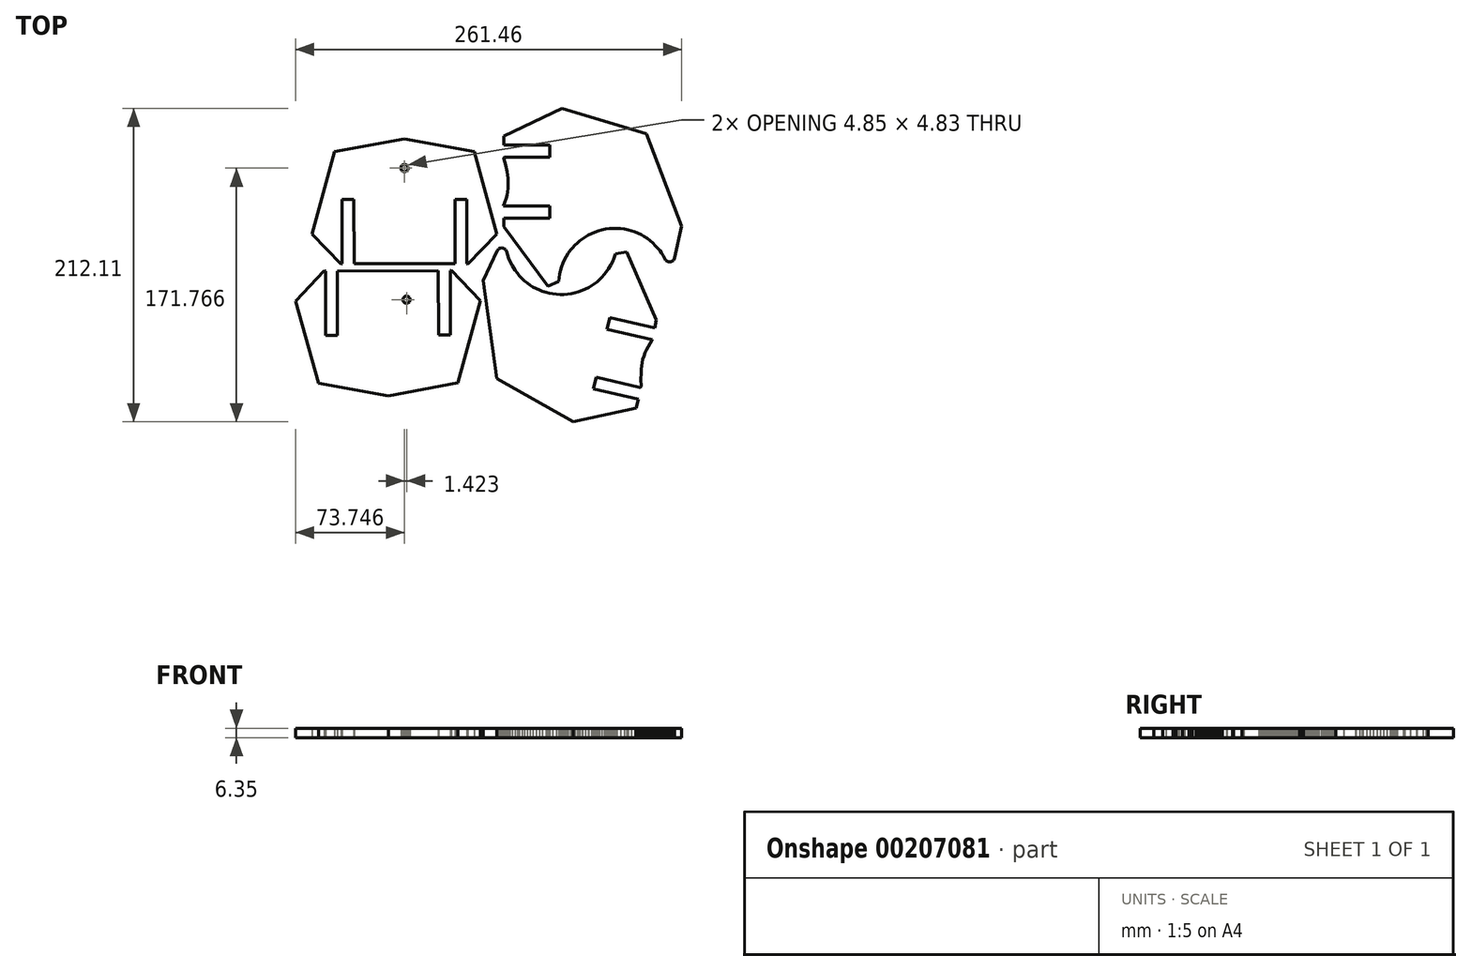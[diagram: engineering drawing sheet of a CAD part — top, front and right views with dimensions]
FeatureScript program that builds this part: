
annotation { "Feature Type Name" : "Feature", "Feature Type Description" : "" }
export const myFeature = defineFeature(function(context is Context, id is Id, definition is map)
    precondition{}
    {
        {
            var Q0;
            Q0=qCreatedBy(makeId("Top.planeOp"),FACE);
            var sketch = newSketch(context, id + "F0", { "sketchPlane" : qUnion([Q0])});
            skLineSegment(sketch, "E0", {"start": v(-798.32, 30.2) * mm, "end": v(-878.98, 30.2) * mm});
            skLineSegment(sketch, "E1", {"start": v(-854.84, 105.1) * mm, "end": v(-865.97, 116.25) * mm});
            skArc(sketch, "E2", {"start": v(-798.32, 30.2) * mm, "mid": v(-791.28, 34.9) * mm, "end": v(-792.93, 43.2) * mm});
            skArc(sketch, "E3", {"start": v(-865.97, 116.25) * mm, "mid": v(-874.28, 117.9) * mm, "end": v(-878.98, 110.86) * mm});
            skLineSegment(sketch, "E4", {"start": v(-878.98, 110.86) * mm, "end": v(-878.98, 30.2) * mm});
            skArc(sketch, "E5", {"start": v(-854.84, 105.1) * mm, "mid": v(-851.3, 103.1) * mm, "end": v(-847.23, 103.2) * mm});
            skArc(sketch, "E6", {"start": v(-805.97, 61.95) * mm, "mid": v(-814.21, 94.96) * mm, "end": v(-847.23, 103.2) * mm});
            skArc(sketch, "E7", {"start": v(-851.35, 42.59) * mm, "mid": v(-846.9, 52.27) * mm, "end": v(-846.27, 62.9) * mm});
            skLineSegment(sketch, "E8", {"start": v(-831.03, 42.59) * mm, "end": v(-851.35, 42.59) * mm});
            skArc(sketch, "E9", {"start": v(-836.11, 62.9) * mm, "mid": v(-835.49, 52.27) * mm, "end": v(-831.03, 42.59) * mm});
            skArc(sketch, "E10", {"start": v(-815.8, 57.83) * mm, "mid": v(-825.47, 62.28) * mm, "end": v(-836.11, 62.9) * mm});
            skLineSegment(sketch, "E11", {"start": v(-815.8, 78.15) * mm, "end": v(-815.8, 57.83) * mm});
            skArc(sketch, "E12", {"start": v(-836.11, 73.07) * mm, "mid": v(-825.47, 73.69) * mm, "end": v(-815.8, 78.15) * mm});
            skArc(sketch, "E13", {"start": v(-831.03, 93.39) * mm, "mid": v(-835.49, 83.7) * mm, "end": v(-836.11, 73.07) * mm});
            skLineSegment(sketch, "E14", {"start": v(-851.35, 93.39) * mm, "end": v(-831.03, 93.39) * mm});
            skArc(sketch, "E15", {"start": v(-846.27, 73.07) * mm, "mid": v(-846.9, 83.7) * mm, "end": v(-851.35, 93.39) * mm});
            skArc(sketch, "E16", {"start": v(-866.6, 78.15) * mm, "mid": v(-856.91, 73.69) * mm, "end": v(-846.27, 73.07) * mm});
            skLineSegment(sketch, "E17", {"start": v(-866.6, 57.83) * mm, "end": v(-866.6, 78.15) * mm});
            skArc(sketch, "E18", {"start": v(-846.27, 62.9) * mm, "mid": v(-856.91, 62.28) * mm, "end": v(-866.6, 57.83) * mm});
            skArc(sketch, "E19", {"start": v(-805.97, 61.95) * mm, "mid": v(-806.07, 57.88) * mm, "end": v(-804.07, 54.34) * mm});
            skLineSegment(sketch, "E20", {"start": v(-804.07, 54.34) * mm, "end": v(-792.93, 43.2) * mm});
            skLineSegment(sketch, "E21", {"start": v(-610.3, 30.2) * mm, "end": v(-699.5, 30.2) * mm});
            skLineSegment(sketch, "E22", {"start": v(-661.26, 120.9) * mm, "end": v(-660.25, 121.09) * mm});
            skLineSegment(sketch, "E23", {"start": v(-660.57, 87.06) * mm, "end": v(-661.8, 88.46) * mm});
            skLineSegment(sketch, "E24", {"start": v(-668.38, 97.43) * mm, "end": v(-660.94, 110.33) * mm});
            skLineSegment(sketch, "E25", {"start": v(-651.07, 70.5) * mm, "end": v(-663.11, 63.55) * mm});
            skLineSegment(sketch, "E26", {"start": v(-661.79, 79.2) * mm, "end": v(-660.35, 77.84) * mm});
            skLineSegment(sketch, "E27", {"start": v(-661.05, 36.54) * mm, "end": v(-674.5, 36.54) * mm});
            skLineSegment(sketch, "E28", {"start": v(-661.84, 38.75) * mm, "end": v(-661.05, 36.54) * mm});
            skLineSegment(sketch, "E29", {"start": v(-712.2, 42.9) * mm, "end": v(-712.2, 132.5) * mm});
            skLineSegment(sketch, "E30", {"start": v(-668.24, 67.85) * mm, "end": v(-669.88, 69.36) * mm});
            skLineSegment(sketch, "E31", {"start": v(-679.21, 69.81) * mm, "end": v(-677.61, 68.1) * mm});
            skLineSegment(sketch, "E32", {"start": v(-689, 61.7) * mm, "end": v(-682.28, 73.35) * mm});
            skLineSegment(sketch, "E33", {"start": v(-705.86, 68) * mm, "end": v(-705.86, 81.45) * mm});
            skLineSegment(sketch, "E34", {"start": v(-687.72, 76.63) * mm, "end": v(-694.45, 64.97) * mm});
            skLineSegment(sketch, "E35", {"start": v(-708.77, 34.2) * mm, "end": v(-709.3, 34.8) * mm});
            skLineSegment(sketch, "E36", {"start": v(-712.1, 41.3) * mm, "end": v(-712.18, 42.1) * mm});
            skLineSegment(sketch, "E37", {"start": v(-710.64, 36.78) * mm, "end": v(-711, 37.49) * mm});
            skLineSegment(sketch, "E38", {"start": v(-710.23, 36.09) * mm, "end": v(-710.64, 36.78) * mm});
            skLineSegment(sketch, "E39", {"start": v(-709.78, 35.43) * mm, "end": v(-710.23, 36.09) * mm});
            skLineSegment(sketch, "E40", {"start": v(-709.3, 34.8) * mm, "end": v(-709.78, 35.43) * mm});
            skLineSegment(sketch, "E41", {"start": v(-711.81, 39.74) * mm, "end": v(-711.98, 40.51) * mm});
            skLineSegment(sketch, "E42", {"start": v(-711.98, 40.51) * mm, "end": v(-712.1, 41.3) * mm});
            skLineSegment(sketch, "E43", {"start": v(-711.59, 38.97) * mm, "end": v(-711.81, 39.74) * mm});
            skLineSegment(sketch, "E44", {"start": v(-711.32, 38.22) * mm, "end": v(-711.59, 38.97) * mm});
            skLineSegment(sketch, "E45", {"start": v(-711, 37.49) * mm, "end": v(-711.32, 38.22) * mm});
            skLineSegment(sketch, "E46", {"start": v(-712.18, 42.1) * mm, "end": v(-712.2, 42.9) * mm});
            skLineSegment(sketch, "E47", {"start": v(-706.97, 32.62) * mm, "end": v(-707.6, 33.1) * mm});
            skLineSegment(sketch, "E48", {"start": v(-702.67, 30.6) * mm, "end": v(-703.43, 30.82) * mm});
            skLineSegment(sketch, "E49", {"start": v(-705.63, 31.76) * mm, "end": v(-706.31, 32.17) * mm});
            skLineSegment(sketch, "E50", {"start": v(-706.31, 32.17) * mm, "end": v(-706.97, 32.62) * mm});
            skLineSegment(sketch, "E51", {"start": v(-704.92, 31.4) * mm, "end": v(-705.63, 31.76) * mm});
            skLineSegment(sketch, "E52", {"start": v(-704.18, 31.09) * mm, "end": v(-704.92, 31.4) * mm});
            skLineSegment(sketch, "E53", {"start": v(-703.43, 30.82) * mm, "end": v(-704.18, 31.09) * mm});
            skLineSegment(sketch, "E54", {"start": v(-699.5, 30.2) * mm, "end": v(-700.3, 30.22) * mm});
            skLineSegment(sketch, "E55", {"start": v(-701.89, 30.42) * mm, "end": v(-702.67, 30.6) * mm});
            skLineSegment(sketch, "E56", {"start": v(-701.1, 30.3) * mm, "end": v(-701.89, 30.42) * mm});
            skLineSegment(sketch, "E57", {"start": v(-700.3, 30.22) * mm, "end": v(-701.1, 30.3) * mm});
            skLineSegment(sketch, "E58", {"start": v(-684.11, 56.62) * mm, "end": v(-685.78, 58.28) * mm});
            skLineSegment(sketch, "E59", {"start": v(-708.2, 33.64) * mm, "end": v(-708.77, 34.2) * mm});
            skLineSegment(sketch, "E60", {"start": v(-707.6, 33.1) * mm, "end": v(-708.2, 33.64) * mm});
            skLineSegment(sketch, "E61", {"start": v(-696.76, 65.48) * mm, "end": v(-699.05, 66.04) * mm});
            skLineSegment(sketch, "E62", {"start": v(-701.34, 66.64) * mm, "end": v(-703.6, 67.3) * mm});
            skLineSegment(sketch, "E63", {"start": v(-703.6, 67.3) * mm, "end": v(-705.86, 68) * mm});
            skLineSegment(sketch, "E64", {"start": v(-699.05, 66.04) * mm, "end": v(-701.34, 66.64) * mm});
            skLineSegment(sketch, "E65", {"start": v(-685.78, 58.28) * mm, "end": v(-687.41, 59.98) * mm});
            skLineSegment(sketch, "E66", {"start": v(-694.45, 64.97) * mm, "end": v(-696.76, 65.48) * mm});
            skLineSegment(sketch, "E67", {"start": v(-687.41, 59.98) * mm, "end": v(-689, 61.7) * mm});
            skLineSegment(sketch, "E68", {"start": v(-677.55, 47.88) * mm, "end": v(-665.9, 54.6) * mm});
            skLineSegment(sketch, "E69", {"start": v(-665.5, 52.3) * mm, "end": v(-665.02, 50) * mm});
            skLineSegment(sketch, "E70", {"start": v(-675.87, 41.04) * mm, "end": v(-676.48, 43.3) * mm});
            skLineSegment(sketch, "E71", {"start": v(-674.5, 36.54) * mm, "end": v(-675.21, 38.78) * mm});
            skLineSegment(sketch, "E72", {"start": v(-675.21, 38.78) * mm, "end": v(-675.87, 41.04) * mm});
            skLineSegment(sketch, "E73", {"start": v(-677.04, 45.59) * mm, "end": v(-677.55, 47.88) * mm});
            skLineSegment(sketch, "E74", {"start": v(-676.48, 43.3) * mm, "end": v(-677.04, 45.59) * mm});
            skLineSegment(sketch, "E75", {"start": v(-663.28, 43.2) * mm, "end": v(-662.59, 40.96) * mm});
            skLineSegment(sketch, "E76", {"start": v(-662.59, 40.96) * mm, "end": v(-661.84, 38.75) * mm});
            skLineSegment(sketch, "E77", {"start": v(-664.5, 47.72) * mm, "end": v(-663.91, 45.46) * mm});
            skLineSegment(sketch, "E78", {"start": v(-663.91, 45.46) * mm, "end": v(-663.28, 43.2) * mm});
            skLineSegment(sketch, "E79", {"start": v(-665.02, 50) * mm, "end": v(-664.5, 47.72) * mm});
            skLineSegment(sketch, "E80", {"start": v(-669.02, 60.14) * mm, "end": v(-680.68, 53.4) * mm});
            skLineSegment(sketch, "E81", {"start": v(-674.29, 64.8) * mm, "end": v(-672.57, 63.2) * mm});
            skLineSegment(sketch, "E82", {"start": v(-682.41, 55) * mm, "end": v(-684.11, 56.62) * mm});
            skLineSegment(sketch, "E83", {"start": v(-680.68, 53.4) * mm, "end": v(-682.41, 55) * mm});
            skLineSegment(sketch, "E84", {"start": v(-677.61, 68.1) * mm, "end": v(-675.97, 66.43) * mm});
            skLineSegment(sketch, "E85", {"start": v(-675.97, 66.43) * mm, "end": v(-674.29, 64.8) * mm});
            skLineSegment(sketch, "E86", {"start": v(-665.9, 54.6) * mm, "end": v(-665.5, 52.3) * mm});
            skLineSegment(sketch, "E87", {"start": v(-666.57, 66.37) * mm, "end": v(-668.24, 67.85) * mm});
            skLineSegment(sketch, "E88", {"start": v(-670.81, 61.65) * mm, "end": v(-669.02, 60.14) * mm});
            skLineSegment(sketch, "E89", {"start": v(-672.57, 63.2) * mm, "end": v(-670.81, 61.65) * mm});
            skLineSegment(sketch, "E90", {"start": v(-663.11, 63.55) * mm, "end": v(-664.86, 64.94) * mm});
            skLineSegment(sketch, "E91", {"start": v(-664.86, 64.94) * mm, "end": v(-666.57, 66.37) * mm});
            skLineSegment(sketch, "E92", {"start": v(-709.16, 135.2) * mm, "end": v(-708.36, 134.41) * mm});
            skLineSegment(sketch, "E93", {"start": v(-712.2, 132.5) * mm, "end": v(-711.43, 133.15) * mm});
            skLineSegment(sketch, "E94", {"start": v(-709.9, 134.5) * mm, "end": v(-709.16, 135.2) * mm});
            skLineSegment(sketch, "E95", {"start": v(-710.66, 133.82) * mm, "end": v(-709.9, 134.5) * mm});
            skLineSegment(sketch, "E96", {"start": v(-711.43, 133.15) * mm, "end": v(-710.66, 133.82) * mm});
            skLineSegment(sketch, "E97", {"start": v(-673.78, 100.78) * mm, "end": v(-666.3, 113.73) * mm});
            skLineSegment(sketch, "E98", {"start": v(-695.65, 104.76) * mm, "end": v(-693.89, 104.17) * mm});
            skLineSegment(sketch, "E99", {"start": v(-683.25, 95.22) * mm, "end": v(-685.2, 95.53) * mm});
            skLineSegment(sketch, "E100", {"start": v(-686.52, 82.87) * mm, "end": v(-684.31, 82.54) * mm});
            skLineSegment(sketch, "E101", {"start": v(-686.7, 102.27) * mm, "end": v(-684.87, 101.92) * mm});
            skLineSegment(sketch, "E102", {"start": v(-701.67, 86.69) * mm, "end": v(-699.55, 85.98) * mm});
            skLineSegment(sketch, "E103", {"start": v(-697.91, 78.87) * mm, "end": v(-695.9, 78.34) * mm});
            skLineSegment(sketch, "E104", {"start": v(-697.41, 85.33) * mm, "end": v(-695.26, 84.73) * mm});
            skLineSegment(sketch, "E105", {"start": v(-703.9, 80.74) * mm, "end": v(-701.91, 80.07) * mm});
            skLineSegment(sketch, "E106", {"start": v(-705.86, 81.45) * mm, "end": v(-703.9, 80.74) * mm});
            skLineSegment(sketch, "E107", {"start": v(-699.92, 79.45) * mm, "end": v(-697.91, 78.87) * mm});
            skLineSegment(sketch, "E108", {"start": v(-701.91, 80.07) * mm, "end": v(-699.92, 79.45) * mm});
            skLineSegment(sketch, "E109", {"start": v(-699.55, 85.98) * mm, "end": v(-697.41, 85.33) * mm});
            skLineSegment(sketch, "E110", {"start": v(-693.87, 77.85) * mm, "end": v(-691.83, 77.4) * mm});
            skLineSegment(sketch, "E111", {"start": v(-691.83, 77.4) * mm, "end": v(-689.78, 77) * mm});
            skLineSegment(sketch, "E112", {"start": v(-689.78, 77) * mm, "end": v(-687.72, 76.63) * mm});
            skLineSegment(sketch, "E113", {"start": v(-693.1, 84.19) * mm, "end": v(-690.91, 83.7) * mm});
            skLineSegment(sketch, "E114", {"start": v(-695.9, 78.34) * mm, "end": v(-693.87, 77.85) * mm});
            skLineSegment(sketch, "E115", {"start": v(-695.26, 84.73) * mm, "end": v(-693.1, 84.19) * mm});
            skLineSegment(sketch, "E116", {"start": v(-688.72, 83.26) * mm, "end": v(-686.52, 82.87) * mm});
            skLineSegment(sketch, "E117", {"start": v(-690.91, 83.7) * mm, "end": v(-688.72, 83.26) * mm});
            skLineSegment(sketch, "E118", {"start": v(-696.7, 98.41) * mm, "end": v(-698.57, 99.06) * mm});
            skLineSegment(sketch, "E119", {"start": v(-705.86, 102.13) * mm, "end": v(-705.86, 88.25) * mm});
            skLineSegment(sketch, "E120", {"start": v(-703.78, 87.45) * mm, "end": v(-701.67, 86.69) * mm});
            skLineSegment(sketch, "E121", {"start": v(-705.86, 88.25) * mm, "end": v(-703.78, 87.45) * mm});
            skLineSegment(sketch, "E122", {"start": v(-702.25, 100.5) * mm, "end": v(-704.07, 101.3) * mm});
            skLineSegment(sketch, "E123", {"start": v(-704.07, 101.3) * mm, "end": v(-705.86, 102.13) * mm});
            skLineSegment(sketch, "E124", {"start": v(-700.42, 99.76) * mm, "end": v(-702.25, 100.5) * mm});
            skLineSegment(sketch, "E125", {"start": v(-698.57, 99.06) * mm, "end": v(-700.42, 99.76) * mm});
            skLineSegment(sketch, "E126", {"start": v(-689.09, 96.3) * mm, "end": v(-691, 96.75) * mm});
            skLineSegment(sketch, "E127", {"start": v(-692.11, 103.63) * mm, "end": v(-690.32, 103.13) * mm});
            skLineSegment(sketch, "E128", {"start": v(-692.92, 97.26) * mm, "end": v(-694.82, 97.81) * mm});
            skLineSegment(sketch, "E129", {"start": v(-694.82, 97.81) * mm, "end": v(-696.7, 98.41) * mm});
            skLineSegment(sketch, "E130", {"start": v(-691, 96.75) * mm, "end": v(-692.92, 97.26) * mm});
            skLineSegment(sketch, "E131", {"start": v(-693.89, 104.17) * mm, "end": v(-692.11, 103.63) * mm});
            skLineSegment(sketch, "E132", {"start": v(-687.15, 95.89) * mm, "end": v(-689.09, 96.3) * mm});
            skLineSegment(sketch, "E133", {"start": v(-685.2, 95.53) * mm, "end": v(-687.15, 95.89) * mm});
            skLineSegment(sketch, "E134", {"start": v(-688.51, 102.68) * mm, "end": v(-686.7, 102.27) * mm});
            skLineSegment(sketch, "E135", {"start": v(-690.32, 103.13) * mm, "end": v(-688.51, 102.68) * mm});
            skLineSegment(sketch, "E136", {"start": v(-669.64, 88.06) * mm, "end": v(-668.42, 86.5) * mm});
            skLineSegment(sketch, "E137", {"start": v(-678.88, 79.25) * mm, "end": v(-671.94, 91.27) * mm});
            skLineSegment(sketch, "E138", {"start": v(-684.31, 82.54) * mm, "end": v(-677.36, 94.59) * mm});
            skLineSegment(sketch, "E139", {"start": v(-673.04, 72.5) * mm, "end": v(-674.56, 74.14) * mm});
            skLineSegment(sketch, "E140", {"start": v(-677.48, 77.51) * mm, "end": v(-678.88, 79.25) * mm});
            skLineSegment(sketch, "E141", {"start": v(-682.28, 73.35) * mm, "end": v(-680.77, 71.56) * mm});
            skLineSegment(sketch, "E142", {"start": v(-680.77, 71.56) * mm, "end": v(-679.21, 69.81) * mm});
            skLineSegment(sketch, "E143", {"start": v(-676.04, 75.8) * mm, "end": v(-677.48, 77.51) * mm});
            skLineSegment(sketch, "E144", {"start": v(-674.56, 74.14) * mm, "end": v(-676.04, 75.8) * mm});
            skLineSegment(sketch, "E145", {"start": v(-669.88, 69.36) * mm, "end": v(-671.48, 70.91) * mm});
            skLineSegment(sketch, "E146", {"start": v(-671.48, 70.91) * mm, "end": v(-673.04, 72.5) * mm});
            skLineSegment(sketch, "E147", {"start": v(-668.42, 86.5) * mm, "end": v(-667.17, 84.98) * mm});
            skLineSegment(sketch, "E148", {"start": v(-665.88, 83.48) * mm, "end": v(-664.55, 82.02) * mm});
            skLineSegment(sketch, "E149", {"start": v(-664.55, 82.02) * mm, "end": v(-663.19, 80.6) * mm});
            skLineSegment(sketch, "E150", {"start": v(-663.19, 80.6) * mm, "end": v(-661.79, 79.2) * mm});
            skLineSegment(sketch, "E151", {"start": v(-667.17, 84.98) * mm, "end": v(-665.88, 83.48) * mm});
            skLineSegment(sketch, "E152", {"start": v(-677.36, 94.59) * mm, "end": v(-679.33, 94.75) * mm});
            skLineSegment(sketch, "E153", {"start": v(-681.3, 94.96) * mm, "end": v(-683.25, 95.22) * mm});
            skLineSegment(sketch, "E154", {"start": v(-679.33, 94.75) * mm, "end": v(-681.3, 94.96) * mm});
            skLineSegment(sketch, "E155", {"start": v(-679.35, 101.13) * mm, "end": v(-677.5, 100.96) * mm});
            skLineSegment(sketch, "E156", {"start": v(-683.04, 101.6) * mm, "end": v(-681.2, 101.35) * mm});
            skLineSegment(sketch, "E157", {"start": v(-684.87, 101.92) * mm, "end": v(-683.04, 101.6) * mm});
            skLineSegment(sketch, "E158", {"start": v(-681.2, 101.35) * mm, "end": v(-679.35, 101.13) * mm});
            skLineSegment(sketch, "E159", {"start": v(-677.5, 100.96) * mm, "end": v(-675.64, 100.85) * mm});
            skLineSegment(sketch, "E160", {"start": v(-675.64, 100.85) * mm, "end": v(-673.78, 100.78) * mm});
            skLineSegment(sketch, "E161", {"start": v(-666.34, 94.33) * mm, "end": v(-667.38, 95.87) * mm});
            skLineSegment(sketch, "E162", {"start": v(-671.94, 91.27) * mm, "end": v(-670.8, 89.65) * mm});
            skLineSegment(sketch, "E163", {"start": v(-670.8, 89.65) * mm, "end": v(-669.64, 88.06) * mm});
            skLineSegment(sketch, "E164", {"start": v(-662.99, 89.88) * mm, "end": v(-664.14, 91.33) * mm});
            skLineSegment(sketch, "E165", {"start": v(-661.8, 88.46) * mm, "end": v(-662.99, 89.88) * mm});
            skLineSegment(sketch, "E166", {"start": v(-664.14, 91.33) * mm, "end": v(-665.26, 92.82) * mm});
            skLineSegment(sketch, "E167", {"start": v(-665.26, 92.82) * mm, "end": v(-666.34, 94.33) * mm});
            skLineSegment(sketch, "E168", {"start": v(-667.38, 95.87) * mm, "end": v(-668.38, 97.43) * mm});
            skLineSegment(sketch, "E169", {"start": v(-686.12, 121.73) * mm, "end": v(-684.57, 121.32) * mm});
            skLineSegment(sketch, "E170", {"start": v(-683.62, 114.6) * mm, "end": v(-685.32, 114.98) * mm});
            skLineSegment(sketch, "E171", {"start": v(-689.2, 122.69) * mm, "end": v(-687.66, 122.19) * mm});
            skLineSegment(sketch, "E172", {"start": v(-705.86, 124.13) * mm, "end": v(-705.86, 109.25) * mm});
            skLineSegment(sketch, "E173", {"start": v(-702.95, 122.22) * mm, "end": v(-704.42, 123.16) * mm});
            skLineSegment(sketch, "E174", {"start": v(-696.82, 118.93) * mm, "end": v(-698.4, 119.68) * mm});
            skLineSegment(sketch, "E175", {"start": v(-697.4, 105.4) * mm, "end": v(-695.65, 104.76) * mm});
            skLineSegment(sketch, "E176", {"start": v(-704.2, 108.4) * mm, "end": v(-702.54, 107.58) * mm});
            skLineSegment(sketch, "E177", {"start": v(-705.86, 109.25) * mm, "end": v(-704.2, 108.4) * mm});
            skLineSegment(sketch, "E178", {"start": v(-700.84, 106.8) * mm, "end": v(-699.13, 106.08) * mm});
            skLineSegment(sketch, "E179", {"start": v(-702.54, 107.58) * mm, "end": v(-700.84, 106.8) * mm});
            skLineSegment(sketch, "E180", {"start": v(-699.13, 106.08) * mm, "end": v(-697.4, 105.4) * mm});
            skLineSegment(sketch, "E181", {"start": v(-701.46, 121.33) * mm, "end": v(-702.95, 122.22) * mm});
            skLineSegment(sketch, "E182", {"start": v(-698.4, 119.68) * mm, "end": v(-699.94, 120.48) * mm});
            skLineSegment(sketch, "E183", {"start": v(-699.94, 120.48) * mm, "end": v(-701.46, 121.33) * mm});
            skLineSegment(sketch, "E184", {"start": v(-690.35, 116.38) * mm, "end": v(-692, 116.94) * mm});
            skLineSegment(sketch, "E185", {"start": v(-693.62, 117.56) * mm, "end": v(-695.23, 118.22) * mm});
            skLineSegment(sketch, "E186", {"start": v(-692, 116.94) * mm, "end": v(-693.62, 117.56) * mm});
            skLineSegment(sketch, "E187", {"start": v(-695.23, 118.22) * mm, "end": v(-696.82, 118.93) * mm});
            skLineSegment(sketch, "E188", {"start": v(-687.01, 115.4) * mm, "end": v(-688.69, 115.86) * mm});
            skLineSegment(sketch, "E189", {"start": v(-688.69, 115.86) * mm, "end": v(-690.35, 116.38) * mm});
            skLineSegment(sketch, "E190", {"start": v(-685.32, 114.98) * mm, "end": v(-687.01, 115.4) * mm});
            skLineSegment(sketch, "E191", {"start": v(-687.66, 122.19) * mm, "end": v(-686.12, 121.73) * mm});
            skLineSegment(sketch, "E192", {"start": v(-697.96, 126.65) * mm, "end": v(-696.55, 125.87) * mm});
            skLineSegment(sketch, "E193", {"start": v(-705.86, 132.13) * mm, "end": v(-704.61, 131.12) * mm});
            skLineSegment(sketch, "E194", {"start": v(-703.34, 130.14) * mm, "end": v(-702.03, 129.2) * mm});
            skLineSegment(sketch, "E195", {"start": v(-704.42, 123.16) * mm, "end": v(-705.86, 124.13) * mm});
            skLineSegment(sketch, "E196", {"start": v(-704.61, 131.12) * mm, "end": v(-703.34, 130.14) * mm});
            skLineSegment(sketch, "E197", {"start": v(-699.34, 127.46) * mm, "end": v(-697.96, 126.65) * mm});
            skLineSegment(sketch, "E198", {"start": v(-700.7, 128.31) * mm, "end": v(-699.34, 127.46) * mm});
            skLineSegment(sketch, "E199", {"start": v(-702.03, 129.2) * mm, "end": v(-700.7, 128.31) * mm});
            skLineSegment(sketch, "E200", {"start": v(-706.7, 132.88) * mm, "end": v(-705.86, 132.13) * mm});
            skLineSegment(sketch, "E201", {"start": v(-707.54, 133.64) * mm, "end": v(-706.7, 132.88) * mm});
            skLineSegment(sketch, "E202", {"start": v(-708.36, 134.41) * mm, "end": v(-707.54, 133.64) * mm});
            skLineSegment(sketch, "E203", {"start": v(-692.2, 123.83) * mm, "end": v(-690.7, 123.23) * mm});
            skLineSegment(sketch, "E204", {"start": v(-695.12, 125.15) * mm, "end": v(-693.67, 124.47) * mm});
            skLineSegment(sketch, "E205", {"start": v(-696.55, 125.87) * mm, "end": v(-695.12, 125.15) * mm});
            skLineSegment(sketch, "E206", {"start": v(-693.67, 124.47) * mm, "end": v(-692.2, 123.83) * mm});
            skLineSegment(sketch, "E207", {"start": v(-690.7, 123.23) * mm, "end": v(-689.2, 122.69) * mm});
            skLineSegment(sketch, "E208", {"start": v(-673.45, 119.82) * mm, "end": v(-671.85, 119.8) * mm});
            skLineSegment(sketch, "E209", {"start": v(-671.52, 113.46) * mm, "end": v(-673.26, 113.47) * mm});
            skLineSegment(sketch, "E210", {"start": v(-679.85, 120.4) * mm, "end": v(-678.26, 120.18) * mm});
            skLineSegment(sketch, "E211", {"start": v(-678.46, 113.8) * mm, "end": v(-680.2, 114.02) * mm});
            skLineSegment(sketch, "E212", {"start": v(-681.91, 114.3) * mm, "end": v(-683.62, 114.6) * mm});
            skLineSegment(sketch, "E213", {"start": v(-680.2, 114.02) * mm, "end": v(-681.91, 114.3) * mm});
            skLineSegment(sketch, "E214", {"start": v(-683, 120.97) * mm, "end": v(-681.43, 120.65) * mm});
            skLineSegment(sketch, "E215", {"start": v(-684.57, 121.32) * mm, "end": v(-683, 120.97) * mm});
            skLineSegment(sketch, "E216", {"start": v(-681.43, 120.65) * mm, "end": v(-679.85, 120.4) * mm});
            skLineSegment(sketch, "E217", {"start": v(-675, 113.53) * mm, "end": v(-676.73, 113.64) * mm});
            skLineSegment(sketch, "E218", {"start": v(-676.73, 113.64) * mm, "end": v(-678.46, 113.8) * mm});
            skLineSegment(sketch, "E219", {"start": v(-673.26, 113.47) * mm, "end": v(-675, 113.53) * mm});
            skLineSegment(sketch, "E220", {"start": v(-676.66, 120) * mm, "end": v(-675.06, 119.9) * mm});
            skLineSegment(sketch, "E221", {"start": v(-678.26, 120.18) * mm, "end": v(-676.66, 120) * mm});
            skLineSegment(sketch, "E222", {"start": v(-675.06, 119.9) * mm, "end": v(-673.45, 119.82) * mm});
            skLineSegment(sketch, "E223", {"start": v(-668.64, 119.91) * mm, "end": v(-667.04, 120.04) * mm});
            skLineSegment(sketch, "E224", {"start": v(-666.3, 113.73) * mm, "end": v(-668.04, 113.59) * mm});
            skLineSegment(sketch, "E225", {"start": v(-669.78, 113.5) * mm, "end": v(-671.52, 113.46) * mm});
            skLineSegment(sketch, "E226", {"start": v(-668.04, 113.59) * mm, "end": v(-669.78, 113.5) * mm});
            skLineSegment(sketch, "E227", {"start": v(-670.24, 119.83) * mm, "end": v(-668.64, 119.91) * mm});
            skLineSegment(sketch, "E228", {"start": v(-671.85, 119.8) * mm, "end": v(-670.24, 119.83) * mm});
            skLineSegment(sketch, "E229", {"start": v(-665.44, 120.22) * mm, "end": v(-663.85, 120.44) * mm});
            skLineSegment(sketch, "E230", {"start": v(-667.04, 120.04) * mm, "end": v(-665.44, 120.22) * mm});
            skLineSegment(sketch, "E231", {"start": v(-662.27, 120.71) * mm, "end": v(-661.26, 120.9) * mm});
            skLineSegment(sketch, "E232", {"start": v(-663.85, 120.44) * mm, "end": v(-662.27, 120.71) * mm});
            skLineSegment(sketch, "E233", {"start": v(-622.8, 70.18) * mm, "end": v(-622.76, 68.54) * mm});
            skLineSegment(sketch, "E234", {"start": v(-629.13, 69.02) * mm, "end": v(-629.05, 67.28) * mm});
            skLineSegment(sketch, "E235", {"start": v(-641.82, 68.51) * mm, "end": v(-628.92, 75.96) * mm});
            skLineSegment(sketch, "E236", {"start": v(-614.47, 42.28) * mm, "end": v(-613.56, 40.91) * mm});
            skLineSegment(sketch, "E237", {"start": v(-637.07, 44.97) * mm, "end": v(-637.72, 46.7) * mm});
            skLineSegment(sketch, "E238", {"start": v(-638.87, 50.24) * mm, "end": v(-639.38, 52.02) * mm});
            skLineSegment(sketch, "E239", {"start": v(-658.33, 49.26) * mm, "end": v(-658.83, 51.43) * mm});
            skLineSegment(sketch, "E240", {"start": v(-645.76, 51.34) * mm, "end": v(-645.25, 49.43) * mm});
            skLineSegment(sketch, "E241", {"start": v(-640.33, 36.54) * mm, "end": v(-654.23, 36.54) * mm});
            skLineSegment(sketch, "E242", {"start": v(-655.8, 40.71) * mm, "end": v(-656.51, 42.82) * mm});
            skLineSegment(sketch, "E243", {"start": v(-655.04, 38.62) * mm, "end": v(-655.8, 40.71) * mm});
            skLineSegment(sketch, "E244", {"start": v(-654.23, 36.54) * mm, "end": v(-655.04, 38.62) * mm});
            skLineSegment(sketch, "E245", {"start": v(-657.17, 44.95) * mm, "end": v(-657.78, 47.1) * mm});
            skLineSegment(sketch, "E246", {"start": v(-656.51, 42.82) * mm, "end": v(-657.17, 44.95) * mm});
            skLineSegment(sketch, "E247", {"start": v(-657.78, 47.1) * mm, "end": v(-658.33, 49.26) * mm});
            skLineSegment(sketch, "E248", {"start": v(-642.72, 41.96) * mm, "end": v(-641.97, 40.13) * mm});
            skLineSegment(sketch, "E249", {"start": v(-641.17, 38.33) * mm, "end": v(-640.33, 36.54) * mm});
            skLineSegment(sketch, "E250", {"start": v(-641.97, 40.13) * mm, "end": v(-641.17, 38.33) * mm});
            skLineSegment(sketch, "E251", {"start": v(-643.42, 43.8) * mm, "end": v(-642.72, 41.96) * mm});
            skLineSegment(sketch, "E252", {"start": v(-644.69, 47.54) * mm, "end": v(-644.08, 45.66) * mm});
            skLineSegment(sketch, "E253", {"start": v(-644.08, 45.66) * mm, "end": v(-643.42, 43.8) * mm});
            skLineSegment(sketch, "E254", {"start": v(-645.25, 49.43) * mm, "end": v(-644.69, 47.54) * mm});
            skLineSegment(sketch, "E255", {"start": v(-638.32, 48.46) * mm, "end": v(-638.87, 50.24) * mm});
            skLineSegment(sketch, "E256", {"start": v(-637.72, 46.7) * mm, "end": v(-638.32, 48.46) * mm});
            skLineSegment(sketch, "E257", {"start": v(-660, 58) * mm, "end": v(-647.99, 64.95) * mm});
            skLineSegment(sketch, "E258", {"start": v(-659.28, 53.61) * mm, "end": v(-659.67, 55.8) * mm});
            skLineSegment(sketch, "E259", {"start": v(-658.83, 51.43) * mm, "end": v(-659.28, 53.61) * mm});
            skLineSegment(sketch, "E260", {"start": v(-659.67, 55.8) * mm, "end": v(-660, 58) * mm});
            skLineSegment(sketch, "E261", {"start": v(-640.94, 59.28) * mm, "end": v(-641.2, 61.11) * mm});
            skLineSegment(sketch, "E262", {"start": v(-647.6, 61.02) * mm, "end": v(-647.33, 59.07) * mm});
            skLineSegment(sketch, "E263", {"start": v(-647.01, 57.12) * mm, "end": v(-646.64, 55.18) * mm});
            skLineSegment(sketch, "E264", {"start": v(-646.64, 55.18) * mm, "end": v(-646.23, 53.25) * mm});
            skLineSegment(sketch, "E265", {"start": v(-646.23, 53.25) * mm, "end": v(-645.76, 51.34) * mm});
            skLineSegment(sketch, "E266", {"start": v(-647.33, 59.07) * mm, "end": v(-647.01, 57.12) * mm});
            skLineSegment(sketch, "E267", {"start": v(-639.84, 53.82) * mm, "end": v(-640.25, 55.63) * mm});
            skLineSegment(sketch, "E268", {"start": v(-639.38, 52.02) * mm, "end": v(-639.84, 53.82) * mm});
            skLineSegment(sketch, "E269", {"start": v(-640.25, 55.63) * mm, "end": v(-640.62, 57.45) * mm});
            skLineSegment(sketch, "E270", {"start": v(-640.62, 57.45) * mm, "end": v(-640.94, 59.28) * mm});
            skLineSegment(sketch, "E271", {"start": v(-647.99, 64.95) * mm, "end": v(-647.82, 62.98) * mm});
            skLineSegment(sketch, "E272", {"start": v(-647.82, 62.98) * mm, "end": v(-647.6, 61.02) * mm});
            skLineSegment(sketch, "E273", {"start": v(-641.43, 62.96) * mm, "end": v(-641.6, 64.8) * mm});
            skLineSegment(sketch, "E274", {"start": v(-641.2, 61.11) * mm, "end": v(-641.43, 62.96) * mm});
            skLineSegment(sketch, "E275", {"start": v(-641.74, 66.66) * mm, "end": v(-641.82, 68.51) * mm});
            skLineSegment(sketch, "E276", {"start": v(-641.6, 64.8) * mm, "end": v(-641.74, 66.66) * mm});
            skLineSegment(sketch, "E277", {"start": v(-618.98, 51) * mm, "end": v(-618.34, 49.5) * mm});
            skLineSegment(sketch, "E278", {"start": v(-626.1, 51.97) * mm, "end": v(-625.53, 50.34) * mm});
            skLineSegment(sketch, "E279", {"start": v(-618.26, 36.54) * mm, "end": v(-633.2, 36.54) * mm});
            skLineSegment(sketch, "E280", {"start": v(-625.53, 50.34) * mm, "end": v(-624.9, 48.71) * mm});
            skLineSegment(sketch, "E281", {"start": v(-635.65, 41.54) * mm, "end": v(-636.39, 43.24) * mm});
            skLineSegment(sketch, "E282", {"start": v(-633.2, 36.54) * mm, "end": v(-634.06, 38.19) * mm});
            skLineSegment(sketch, "E283", {"start": v(-634.06, 38.19) * mm, "end": v(-634.88, 39.85) * mm});
            skLineSegment(sketch, "E284", {"start": v(-634.88, 39.85) * mm, "end": v(-635.65, 41.54) * mm});
            skLineSegment(sketch, "E285", {"start": v(-636.39, 43.24) * mm, "end": v(-637.07, 44.97) * mm});
            skLineSegment(sketch, "E286", {"start": v(-621.94, 42.43) * mm, "end": v(-621.08, 40.92) * mm});
            skLineSegment(sketch, "E287", {"start": v(-620.18, 39.43) * mm, "end": v(-619.24, 37.97) * mm});
            skLineSegment(sketch, "E288", {"start": v(-621.08, 40.92) * mm, "end": v(-620.18, 39.43) * mm});
            skLineSegment(sketch, "E289", {"start": v(-619.24, 37.97) * mm, "end": v(-618.26, 36.54) * mm});
            skLineSegment(sketch, "E290", {"start": v(-624.23, 47.11) * mm, "end": v(-623.51, 45.53) * mm});
            skLineSegment(sketch, "E291", {"start": v(-622.75, 43.97) * mm, "end": v(-621.94, 42.43) * mm});
            skLineSegment(sketch, "E292", {"start": v(-623.51, 45.53) * mm, "end": v(-622.75, 43.97) * mm});
            skLineSegment(sketch, "E293", {"start": v(-624.9, 48.71) * mm, "end": v(-624.23, 47.11) * mm});
            skLineSegment(sketch, "E294", {"start": v(-616.93, 46.53) * mm, "end": v(-616.15, 45.09) * mm});
            skLineSegment(sketch, "E295", {"start": v(-615.33, 43.67) * mm, "end": v(-614.47, 42.28) * mm});
            skLineSegment(sketch, "E296", {"start": v(-616.15, 45.09) * mm, "end": v(-615.33, 43.67) * mm});
            skLineSegment(sketch, "E297", {"start": v(-617.66, 48) * mm, "end": v(-616.93, 46.53) * mm});
            skLineSegment(sketch, "E298", {"start": v(-618.34, 49.5) * mm, "end": v(-617.66, 48) * mm});
            skLineSegment(sketch, "E299", {"start": v(-628.24, 60.38) * mm, "end": v(-627.91, 58.68) * mm});
            skLineSegment(sketch, "E300", {"start": v(-627.54, 56.98) * mm, "end": v(-627.1, 55.3) * mm});
            skLineSegment(sketch, "E301", {"start": v(-626.63, 53.63) * mm, "end": v(-626.1, 51.97) * mm});
            skLineSegment(sketch, "E302", {"start": v(-627.1, 55.3) * mm, "end": v(-626.63, 53.63) * mm});
            skLineSegment(sketch, "E303", {"start": v(-627.91, 58.68) * mm, "end": v(-627.54, 56.98) * mm});
            skLineSegment(sketch, "E304", {"start": v(-628.93, 65.55) * mm, "end": v(-628.75, 63.82) * mm});
            skLineSegment(sketch, "E305", {"start": v(-628.52, 62.1) * mm, "end": v(-628.24, 60.38) * mm});
            skLineSegment(sketch, "E306", {"start": v(-628.75, 63.82) * mm, "end": v(-628.52, 62.1) * mm});
            skLineSegment(sketch, "E307", {"start": v(-629.05, 67.28) * mm, "end": v(-628.93, 65.55) * mm});
            skLineSegment(sketch, "E308", {"start": v(-621.79, 60.41) * mm, "end": v(-621.44, 58.8) * mm});
            skLineSegment(sketch, "E309", {"start": v(-619.57, 52.53) * mm, "end": v(-618.98, 51) * mm});
            skLineSegment(sketch, "E310", {"start": v(-620.6, 55.64) * mm, "end": v(-620.1, 54.08) * mm});
            skLineSegment(sketch, "E311", {"start": v(-620.1, 54.08) * mm, "end": v(-619.57, 52.53) * mm});
            skLineSegment(sketch, "E312", {"start": v(-621.05, 57.22) * mm, "end": v(-620.6, 55.64) * mm});
            skLineSegment(sketch, "E313", {"start": v(-621.44, 58.8) * mm, "end": v(-621.05, 57.22) * mm});
            skLineSegment(sketch, "E314", {"start": v(-622.52, 65.27) * mm, "end": v(-622.33, 63.64) * mm});
            skLineSegment(sketch, "E315", {"start": v(-622.08, 62.02) * mm, "end": v(-621.79, 60.41) * mm});
            skLineSegment(sketch, "E316", {"start": v(-622.33, 63.64) * mm, "end": v(-622.08, 62.02) * mm});
            skLineSegment(sketch, "E317", {"start": v(-622.66, 66.9) * mm, "end": v(-622.52, 65.27) * mm});
            skLineSegment(sketch, "E318", {"start": v(-622.76, 68.54) * mm, "end": v(-622.66, 66.9) * mm});
            skLineSegment(sketch, "E319", {"start": v(-607.27, 33.37) * mm, "end": v(-610.3, 30.2) * mm});
            skLineSegment(sketch, "E320", {"start": v(-608.42, 34.54) * mm, "end": v(-607.27, 33.37) * mm});
            skLineSegment(sketch, "E321", {"start": v(-611.62, 38.27) * mm, "end": v(-610.6, 37) * mm});
            skLineSegment(sketch, "E322", {"start": v(-609.52, 35.75) * mm, "end": v(-608.42, 34.54) * mm});
            skLineSegment(sketch, "E323", {"start": v(-610.6, 37) * mm, "end": v(-609.52, 35.75) * mm});
            skLineSegment(sketch, "E324", {"start": v(-612.61, 39.57) * mm, "end": v(-611.62, 38.27) * mm});
            skLineSegment(sketch, "E325", {"start": v(-613.56, 40.91) * mm, "end": v(-612.61, 39.57) * mm});
            skLineSegment(sketch, "E326", {"start": v(-650.22, 104.53) * mm, "end": v(-649.27, 103.24) * mm});
            skLineSegment(sketch, "E327", {"start": v(-658.53, 105.7) * mm, "end": v(-657.64, 104.21) * mm});
            skLineSegment(sketch, "E328", {"start": v(-637.75, 92.17) * mm, "end": v(-636.43, 91.27) * mm});
            skLineSegment(sketch, "E329", {"start": v(-631.94, 81.55) * mm, "end": v(-644.88, 74.07) * mm});
            skLineSegment(sketch, "E330", {"start": v(-638.08, 84.8) * mm, "end": v(-636.58, 83.92) * mm});
            skLineSegment(sketch, "E331", {"start": v(-659.3, 85.7) * mm, "end": v(-660.57, 87.06) * mm});
            skLineSegment(sketch, "E332", {"start": v(-641, 86.69) * mm, "end": v(-639.55, 85.72) * mm});
            skLineSegment(sketch, "E333", {"start": v(-648, 76.1) * mm, "end": v(-649.52, 77.16) * mm});
            skLineSegment(sketch, "E334", {"start": v(-649.52, 77.16) * mm, "end": v(-651, 78.27) * mm});
            skLineSegment(sketch, "E335", {"start": v(-660.35, 77.84) * mm, "end": v(-658.89, 76.52) * mm});
            skLineSegment(sketch, "E336", {"start": v(-655.85, 74) * mm, "end": v(-654.29, 72.8) * mm});
            skLineSegment(sketch, "E337", {"start": v(-658.89, 76.52) * mm, "end": v(-657.38, 75.24) * mm});
            skLineSegment(sketch, "E338", {"start": v(-657.38, 75.24) * mm, "end": v(-655.85, 74) * mm});
            skLineSegment(sketch, "E339", {"start": v(-652.7, 71.63) * mm, "end": v(-651.07, 70.5) * mm});
            skLineSegment(sketch, "E340", {"start": v(-654.29, 72.8) * mm, "end": v(-652.7, 71.63) * mm});
            skLineSegment(sketch, "E341", {"start": v(-653.9, 80.6) * mm, "end": v(-655.3, 81.83) * mm});
            skLineSegment(sketch, "E342", {"start": v(-655.3, 81.83) * mm, "end": v(-656.67, 83.08) * mm});
            skLineSegment(sketch, "E343", {"start": v(-658, 84.38) * mm, "end": v(-659.3, 85.7) * mm});
            skLineSegment(sketch, "E344", {"start": v(-656.67, 83.08) * mm, "end": v(-658, 84.38) * mm});
            skLineSegment(sketch, "E345", {"start": v(-651, 78.27) * mm, "end": v(-652.47, 79.42) * mm});
            skLineSegment(sketch, "E346", {"start": v(-652.47, 79.42) * mm, "end": v(-653.9, 80.6) * mm});
            skLineSegment(sketch, "E347", {"start": v(-644.88, 74.07) * mm, "end": v(-646.45, 75.06) * mm});
            skLineSegment(sketch, "E348", {"start": v(-646.45, 75.06) * mm, "end": v(-648, 76.1) * mm});
            skLineSegment(sketch, "E349", {"start": v(-639.55, 85.72) * mm, "end": v(-638.08, 84.8) * mm});
            skLineSegment(sketch, "E350", {"start": v(-650.22, 94.59) * mm, "end": v(-649, 93.35) * mm});
            skLineSegment(sketch, "E351", {"start": v(-651.4, 95.87) * mm, "end": v(-650.22, 94.59) * mm});
            skLineSegment(sketch, "E352", {"start": v(-655.72, 101.3) * mm, "end": v(-654.7, 99.9) * mm});
            skLineSegment(sketch, "E353", {"start": v(-656.7, 102.75) * mm, "end": v(-655.72, 101.3) * mm});
            skLineSegment(sketch, "E354", {"start": v(-657.64, 104.21) * mm, "end": v(-656.7, 102.75) * mm});
            skLineSegment(sketch, "E355", {"start": v(-652.54, 97.18) * mm, "end": v(-651.4, 95.87) * mm});
            skLineSegment(sketch, "E356", {"start": v(-653.64, 98.52) * mm, "end": v(-652.54, 97.18) * mm});
            skLineSegment(sketch, "E357", {"start": v(-654.7, 99.9) * mm, "end": v(-653.64, 98.52) * mm});
            skLineSegment(sketch, "E358", {"start": v(-642.76, 96.17) * mm, "end": v(-641.55, 95.11) * mm});
            skLineSegment(sketch, "E359", {"start": v(-643.8, 88.75) * mm, "end": v(-642.41, 87.7) * mm});
            skLineSegment(sketch, "E360", {"start": v(-647.76, 92.14) * mm, "end": v(-646.47, 90.97) * mm});
            skLineSegment(sketch, "E361", {"start": v(-646.47, 90.97) * mm, "end": v(-645.15, 89.84) * mm});
            skLineSegment(sketch, "E362", {"start": v(-645.15, 89.84) * mm, "end": v(-643.8, 88.75) * mm});
            skLineSegment(sketch, "E363", {"start": v(-649, 93.35) * mm, "end": v(-647.76, 92.14) * mm});
            skLineSegment(sketch, "E364", {"start": v(-642.41, 87.7) * mm, "end": v(-641, 86.69) * mm});
            skLineSegment(sketch, "E365", {"start": v(-641.55, 95.11) * mm, "end": v(-640.32, 94.1) * mm});
            skLineSegment(sketch, "E366", {"start": v(-639.05, 93.11) * mm, "end": v(-637.75, 92.17) * mm});
            skLineSegment(sketch, "E367", {"start": v(-640.32, 94.1) * mm, "end": v(-639.05, 93.11) * mm});
            skLineSegment(sketch, "E368", {"start": v(-643.93, 97.27) * mm, "end": v(-642.76, 96.17) * mm});
            skLineSegment(sketch, "E369", {"start": v(-647.24, 100.75) * mm, "end": v(-646.18, 99.56) * mm});
            skLineSegment(sketch, "E370", {"start": v(-645.07, 98.4) * mm, "end": v(-643.93, 97.27) * mm});
            skLineSegment(sketch, "E371", {"start": v(-646.18, 99.56) * mm, "end": v(-645.07, 98.4) * mm});
            skLineSegment(sketch, "E372", {"start": v(-648.28, 101.98) * mm, "end": v(-647.24, 100.75) * mm});
            skLineSegment(sketch, "E373", {"start": v(-649.27, 103.24) * mm, "end": v(-648.28, 101.98) * mm});
            skLineSegment(sketch, "E374", {"start": v(-627.95, 86.73) * mm, "end": v(-626.47, 86.13) * mm});
            skLineSegment(sketch, "E375", {"start": v(-626.47, 86.13) * mm, "end": v(-624.96, 85.57) * mm});
            skLineSegment(sketch, "E376", {"start": v(-629.04, 74.23) * mm, "end": v(-629.12, 72.5) * mm});
            skLineSegment(sketch, "E377", {"start": v(-629.15, 70.75) * mm, "end": v(-629.13, 69.02) * mm});
            skLineSegment(sketch, "E378", {"start": v(-629.12, 72.5) * mm, "end": v(-629.15, 70.75) * mm});
            skLineSegment(sketch, "E379", {"start": v(-628.92, 75.96) * mm, "end": v(-629.04, 74.23) * mm});
            skLineSegment(sketch, "E380", {"start": v(-633.5, 82.3) * mm, "end": v(-631.94, 81.55) * mm});
            skLineSegment(sketch, "E381", {"start": v(-635.06, 83.08) * mm, "end": v(-633.5, 82.3) * mm});
            skLineSegment(sketch, "E382", {"start": v(-636.58, 83.92) * mm, "end": v(-635.06, 83.08) * mm});
            skLineSegment(sketch, "E383", {"start": v(-622.24, 78.35) * mm, "end": v(-622.45, 76.72) * mm});
            skLineSegment(sketch, "E384", {"start": v(-622.73, 73.46) * mm, "end": v(-622.79, 71.82) * mm});
            skLineSegment(sketch, "E385", {"start": v(-622.79, 71.82) * mm, "end": v(-622.8, 70.18) * mm});
            skLineSegment(sketch, "E386", {"start": v(-622.45, 76.72) * mm, "end": v(-622.62, 75.1) * mm});
            skLineSegment(sketch, "E387", {"start": v(-622.62, 75.1) * mm, "end": v(-622.73, 73.46) * mm});
            skLineSegment(sketch, "E388", {"start": v(-621.27, 83.19) * mm, "end": v(-621.53, 82.12) * mm});
            skLineSegment(sketch, "E389", {"start": v(-621.98, 79.97) * mm, "end": v(-622.24, 78.35) * mm});
            skLineSegment(sketch, "E390", {"start": v(-621.76, 81.04) * mm, "end": v(-621.98, 79.97) * mm});
            skLineSegment(sketch, "E391", {"start": v(-621.53, 82.12) * mm, "end": v(-621.76, 81.04) * mm});
            skLineSegment(sketch, "E392", {"start": v(-622.99, 84.87) * mm, "end": v(-621.99, 84.55) * mm});
            skLineSegment(sketch, "E393", {"start": v(-623.98, 85.21) * mm, "end": v(-622.99, 84.87) * mm});
            skLineSegment(sketch, "E394", {"start": v(-624.96, 85.57) * mm, "end": v(-623.98, 85.21) * mm});
            skLineSegment(sketch, "E395", {"start": v(-620.99, 84.25) * mm, "end": v(-621.27, 83.19) * mm});
            skLineSegment(sketch, "E396", {"start": v(-621.99, 84.55) * mm, "end": v(-620.99, 84.25) * mm});
            skLineSegment(sketch, "E397", {"start": v(-632.3, 88.8) * mm, "end": v(-630.87, 88.07) * mm});
            skLineSegment(sketch, "E398", {"start": v(-636.43, 91.27) * mm, "end": v(-635.07, 90.4) * mm});
            skLineSegment(sketch, "E399", {"start": v(-635.07, 90.4) * mm, "end": v(-633.7, 89.58) * mm});
            skLineSegment(sketch, "E400", {"start": v(-633.7, 89.58) * mm, "end": v(-632.3, 88.8) * mm});
            skLineSegment(sketch, "E401", {"start": v(-629.42, 87.38) * mm, "end": v(-627.95, 86.73) * mm});
            skLineSegment(sketch, "E402", {"start": v(-630.87, 88.07) * mm, "end": v(-629.42, 87.38) * mm});
            skLineSegment(sketch, "E403", {"start": v(-655.75, 114.28) * mm, "end": v(-655.09, 112.82) * mm});
            skLineSegment(sketch, "E404", {"start": v(-660.94, 110.33) * mm, "end": v(-660.18, 108.76) * mm});
            skLineSegment(sketch, "E405", {"start": v(-659.38, 107.22) * mm, "end": v(-658.53, 105.7) * mm});
            skLineSegment(sketch, "E406", {"start": v(-660.18, 108.76) * mm, "end": v(-659.38, 107.22) * mm});
            skLineSegment(sketch, "E407", {"start": v(-653.64, 109.96) * mm, "end": v(-652.85, 108.56) * mm});
            skLineSegment(sketch, "E408", {"start": v(-652.85, 108.56) * mm, "end": v(-652.01, 107.2) * mm});
            skLineSegment(sketch, "E409", {"start": v(-651.14, 105.85) * mm, "end": v(-650.22, 104.53) * mm});
            skLineSegment(sketch, "E410", {"start": v(-652.01, 107.2) * mm, "end": v(-651.14, 105.85) * mm});
            skLineSegment(sketch, "E411", {"start": v(-654.38, 111.38) * mm, "end": v(-653.64, 109.96) * mm});
            skLineSegment(sketch, "E412", {"start": v(-655.09, 112.82) * mm, "end": v(-654.38, 111.38) * mm});
            skLineSegment(sketch, "E413", {"start": v(-657.3, 118.32) * mm, "end": v(-656.93, 117.26) * mm});
            skLineSegment(sketch, "E414", {"start": v(-656.36, 115.76) * mm, "end": v(-655.75, 114.28) * mm});
            skLineSegment(sketch, "E415", {"start": v(-656.93, 117.26) * mm, "end": v(-656.36, 115.76) * mm});
            skLineSegment(sketch, "E416", {"start": v(-658.25, 121.54) * mm, "end": v(-657.95, 120.46) * mm});
            skLineSegment(sketch, "E417", {"start": v(-659.25, 121.3) * mm, "end": v(-658.25, 121.54) * mm});
            skLineSegment(sketch, "E418", {"start": v(-660.25, 121.09) * mm, "end": v(-659.25, 121.3) * mm});
            skLineSegment(sketch, "E419", {"start": v(-657.63, 119.39) * mm, "end": v(-657.3, 118.32) * mm});
            skLineSegment(sketch, "E420", {"start": v(-657.95, 120.46) * mm, "end": v(-657.63, 119.39) * mm});
            skLineSegment(sketch, "E421", {"start": v(-738.78, 413.69) * mm, "end": v(-816.63, 413.74) * mm});
            skLineSegment(sketch, "E422", {"start": v(-948.3, 377.2) * mm, "end": v(-788.52, 217.4) * mm});
            skLineSegment(sketch, "E423", {"start": v(-739.96, 386.58) * mm, "end": v(-815.5, 386.63) * mm});
            skLineSegment(sketch, "E424", {"start": v(-816.77, 285.21) * mm, "end": v(-740.08, 285.16) * mm});
            skArc(sketch, "E425", {"start": v(-816.77, 285.21) * mm, "mid": v(-796.51, 296.77) * mm, "end": v(-793.62, 319.92) * mm});
            skArc(sketch, "E426", {"start": v(-793.61, 351.87) * mm, "mid": v(-796.48, 374.99) * mm, "end": v(-816.65, 386.64) * mm});
            skLineSegment(sketch, "E427", {"start": v(-828.47, 373.72) * mm, "end": v(-828.6, 295.21) * mm});
            skArc(sketch, "E428", {"start": v(-793.62, 319.92) * mm, "mid": v(-816.74, 317.12) * mm, "end": v(-828.53, 297.03) * mm});
            skLineSegment(sketch, "E429", {"start": v(-831.5, 398.87) * mm, "end": v(-939.33, 398.87) * mm});
            skArc(sketch, "E430", {"start": v(-939.33, 398.87) * mm, "mid": v(-951.06, 391.03) * mm, "end": v(-948.3, 377.2) * mm});
            skArc(sketch, "E431", {"start": v(-828.47, 374.88) * mm, "mid": v(-816.77, 354.7) * mm, "end": v(-793.61, 351.87) * mm});
            skLineSegment(sketch, "E432", {"start": v(-816.63, 413.74) * mm, "end": v(-831.5, 398.87) * mm});
            skLineSegment(sketch, "E433", {"start": v(-767.13, 217.4) * mm, "end": v(-607.33, 377.2) * mm});
            skLineSegment(sketch, "E434", {"start": v(-727.1, 296.91) * mm, "end": v(-727.05, 374.76) * mm});
            skArc(sketch, "E435", {"start": v(-727.1, 296.91) * mm, "mid": v(-738.9, 316.95) * mm, "end": v(-761.96, 319.92) * mm});
            skLineSegment(sketch, "E436", {"start": v(-788.52, 217.4) * mm, "end": v(-767.13, 217.4) * mm});
            skArc(sketch, "E437", {"start": v(-761.96, 319.92) * mm, "mid": v(-759.1, 296.8) * mm, "end": v(-738.93, 285.16) * mm});
            skLineSegment(sketch, "E438", {"start": v(-616.32, 398.87) * mm, "end": v(-723.97, 398.87) * mm});
            skArc(sketch, "E439", {"start": v(-761.97, 351.87) * mm, "mid": v(-739.33, 354.36) * mm, "end": v(-727.16, 373.61) * mm});
            skArc(sketch, "E440", {"start": v(-738.8, 386.58) * mm, "mid": v(-759.07, 375.02) * mm, "end": v(-761.97, 351.87) * mm});
            skLineSegment(sketch, "E441", {"start": v(-723.97, 398.87) * mm, "end": v(-738.78, 413.69) * mm});
            skArc(sketch, "E442", {"start": v(-607.33, 377.2) * mm, "mid": v(-604.58, 391.03) * mm, "end": v(-616.32, 398.87) * mm});
            skLineSegment(sketch, "E443", {"start": v(-543.12, 109.99) * mm, "end": v(-543.12, 92.14) * mm});
            skArc(sketch, "E444", {"start": v(-543.12, 92.14) * mm, "mid": v(-538.63, 94.83) * mm, "end": v(-534.51, 98.08) * mm});
            skArc(sketch, "E445", {"start": v(-529.5, 98.03) * mm, "mid": v(-517.47, 90.2) * mm, "end": v(-503.48, 86.94) * mm});
            skArc(sketch, "E446", {"start": v(-487.7, 95.38) * mm, "mid": v(-481.99, 75.35) * mm, "end": v(-472.24, 56.95) * mm});
            skArc(sketch, "E447", {"start": v(-483.3, 99.7) * mm, "mid": v(-471.75, 65.13) * mm, "end": v(-449.14, 36.54) * mm});
            skLineSegment(sketch, "E448", {"start": v(-503.48, 86.94) * mm, "end": v(-491.21, 98.96) * mm});
            skLineSegment(sketch, "E449", {"start": v(-499.97, 83.36) * mm, "end": v(-487.7, 95.38) * mm});
            skLineSegment(sketch, "E450", {"start": v(-550.74, 138.14) * mm, "end": v(-550.74, 42.9) * mm});
            skLineSegment(sketch, "E451", {"start": v(-495.28, 44.16) * mm, "end": v(-477.22, 44.16) * mm});
            skArc(sketch, "E452", {"start": v(-489.47, 52.1) * mm, "mid": v(-492.6, 48.3) * mm, "end": v(-495.28, 44.16) * mm});
            skArc(sketch, "E453", {"start": v(-499.97, 83.36) * mm, "mid": v(-497, 69.31) * mm, "end": v(-489.41, 57.12) * mm});
            skLineSegment(sketch, "E454", {"start": v(-544.4, 36.54) * mm, "end": v(-449.14, 36.54) * mm});
            skArc(sketch, "E455", {"start": v(-472.29, 51.94) * mm, "mid": v(-474.84, 48.1) * mm, "end": v(-477.22, 44.16) * mm});
            skLineSegment(sketch, "E456", {"start": v(-489.41, 57.12) * mm, "end": v(-472.24, 56.95) * mm});
            skLineSegment(sketch, "E457", {"start": v(-489.47, 52.1) * mm, "end": v(-472.29, 51.94) * mm});
            skArc(sketch, "E458", {"start": v(-495.97, 52.17) * mm, "mid": v(-498.66, 48.3) * mm, "end": v(-500.93, 44.16) * mm});
            skArc(sketch, "E459", {"start": v(-510.82, 52.32) * mm, "mid": v(-514.59, 49) * mm, "end": v(-515.97, 44.16) * mm});
            skLineSegment(sketch, "E460", {"start": v(-515.97, 44.16) * mm, "end": v(-500.93, 44.16) * mm});
            skArc(sketch, "E461", {"start": v(-550.74, 42.9) * mm, "mid": v(-548.88, 38.4) * mm, "end": v(-544.4, 36.54) * mm});
            skArc(sketch, "E462", {"start": v(-529.57, 91.52) * mm, "mid": v(-519.43, 85.59) * mm, "end": v(-508.13, 82.38) * mm});
            skArc(sketch, "E463", {"start": v(-529.8, 69.16) * mm, "mid": v(-527.08, 67.63) * mm, "end": v(-524.1, 66.73) * mm});
            skArc(sketch, "E464", {"start": v(-529.72, 76.67) * mm, "mid": v(-525.12, 72.24) * mm, "end": v(-518.73, 72) * mm});
            skLineSegment(sketch, "E465", {"start": v(-529.88, 61.07) * mm, "end": v(-524.1, 66.73) * mm});
            skArc(sketch, "E466", {"start": v(-504.62, 78.8) * mm, "mid": v(-501.65, 67.44) * mm, "end": v(-495.92, 57.19) * mm});
            skLineSegment(sketch, "E467", {"start": v(-515.23, 68.41) * mm, "end": v(-504.62, 78.8) * mm});
            skLineSegment(sketch, "E468", {"start": v(-510.77, 57.34) * mm, "end": v(-495.92, 57.19) * mm});
            skLineSegment(sketch, "E469", {"start": v(-510.82, 52.32) * mm, "end": v(-495.97, 52.17) * mm});
            skArc(sketch, "E470", {"start": v(-520.6, 63.15) * mm, "mid": v(-519.76, 60.15) * mm, "end": v(-518.28, 57.41) * mm});
            skArc(sketch, "E471", {"start": v(-515.23, 68.41) * mm, "mid": v(-515.1, 62.02) * mm, "end": v(-510.77, 57.34) * mm});
            skLineSegment(sketch, "E472", {"start": v(-526.37, 57.5) * mm, "end": v(-520.6, 63.15) * mm});
            skArc(sketch, "E473", {"start": v(-518.33, 52.4) * mm, "mid": v(-519.86, 49.69) * mm, "end": v(-520.76, 46.7) * mm});
            skLineSegment(sketch, "E474", {"start": v(-526.37, 57.5) * mm, "end": v(-518.28, 57.41) * mm});
            skLineSegment(sketch, "E475", {"start": v(-526.42, 52.48) * mm, "end": v(-518.33, 52.4) * mm});
            skLineSegment(sketch, "E476", {"start": v(-526.42, 52.48) * mm, "end": v(-520.76, 46.7) * mm});
            skLineSegment(sketch, "E477", {"start": v(-518.73, 72) * mm, "end": v(-508.13, 82.38) * mm});
            skArc(sketch, "E478", {"start": v(-540.55, 66.9) * mm, "mid": v(-537.55, 67.73) * mm, "end": v(-534.8, 69.2) * mm});
            skLineSegment(sketch, "E479", {"start": v(-534.89, 61.12) * mm, "end": v(-540.55, 66.9) * mm});
            skLineSegment(sketch, "E480", {"start": v(-534.89, 61.12) * mm, "end": v(-534.8, 69.2) * mm});
            skLineSegment(sketch, "E481", {"start": v(-529.88, 61.07) * mm, "end": v(-529.8, 69.16) * mm});
            skLineSegment(sketch, "E482", {"start": v(-543.12, 86.57) * mm, "end": v(-543.12, 71.74) * mm});
            skLineSegment(sketch, "E483", {"start": v(-534.73, 76.72) * mm, "end": v(-534.58, 91.57) * mm});
            skLineSegment(sketch, "E484", {"start": v(-529.72, 76.67) * mm, "end": v(-529.57, 91.52) * mm});
            skArc(sketch, "E485", {"start": v(-543.12, 71.74) * mm, "mid": v(-538.19, 72.99) * mm, "end": v(-534.73, 76.72) * mm});
            skArc(sketch, "E486", {"start": v(-543.12, 86.57) * mm, "mid": v(-538.72, 88.84) * mm, "end": v(-534.58, 91.57) * mm});
            skArc(sketch, "E487", {"start": v(-529.33, 115.2) * mm, "mid": v(-511.12, 105.08) * mm, "end": v(-491.21, 98.96) * mm});
            skArc(sketch, "E488", {"start": v(-550.74, 138.14) * mm, "mid": v(-521.6, 115.55) * mm, "end": v(-486.82, 103.27) * mm});
            skArc(sketch, "E489", {"start": v(-483.3, 99.7) * mm, "mid": v(-484.5, 102.04) * mm, "end": v(-486.82, 103.27) * mm});
            skLineSegment(sketch, "E490", {"start": v(-534.51, 98.08) * mm, "end": v(-534.34, 115.25) * mm});
            skLineSegment(sketch, "E491", {"start": v(-529.5, 98.03) * mm, "end": v(-529.33, 115.2) * mm});
            skArc(sketch, "E492", {"start": v(-543.12, 109.99) * mm, "mid": v(-538.66, 112.5) * mm, "end": v(-534.34, 115.25) * mm});
            skLineSegment(sketch, "E493", {"start": v(-483.52, 200.4) * mm, "end": v(-483.52, 210.06) * mm});
            skLineSegment(sketch, "E494", {"start": v(-483.52, 210.06) * mm, "end": v(-483.52, 198.16) * mm});
            skLineSegment(sketch, "E495", {"start": v(-483.52, 198.16) * mm, "end": v(-483.52, 198.2) * mm});
            skLineSegment(sketch, "E496", {"start": v(-483.52, 198.2) * mm, "end": v(-483.52, 198.16) * mm});
            skLineSegment(sketch, "E497", {"start": v(-483.52, 198.16) * mm, "end": v(-590.04, 198.16) * mm});
            skLineSegment(sketch, "E498", {"start": v(-590.04, 198.16) * mm, "end": v(-590.04, 304.67) * mm});
            skLineSegment(sketch, "E499", {"start": v(-590.04, 304.67) * mm, "end": v(-578.13, 304.67) * mm});
            skLineSegment(sketch, "E500", {"start": v(-578.13, 304.67) * mm, "end": v(-483.52, 210.06) * mm});
            skLineSegment(sketch, "E501", {"start": v(-545.48, 252.93) * mm, "end": v(-544.49, 253.7) * mm});
            skArc(sketch, "E502", {"start": v(-544.49, 253.7) * mm, "mid": v(-543.5, 256.58) * mm, "end": v(-544.15, 259.56) * mm});
            skArc(sketch, "E503", {"start": v(-544.15, 259.56) * mm, "mid": v(-544.9, 260.94) * mm, "end": v(-545.8, 262.23) * mm});
            skArc(sketch, "E504", {"start": v(-545.8, 262.23) * mm, "mid": v(-547, 263.57) * mm, "end": v(-548.45, 264.63) * mm});
            skArc(sketch, "E505", {"start": v(-548.45, 264.63) * mm, "mid": v(-549.54, 264.96) * mm, "end": v(-550.69, 265.05) * mm});
            skLineSegment(sketch, "E506", {"start": v(-550.69, 265.05) * mm, "end": v(-553.07, 265) * mm});
            skArc(sketch, "E507", {"start": v(-553.07, 265) * mm, "mid": v(-555.16, 264.94) * mm, "end": v(-557.24, 264.73) * mm});
            skArc(sketch, "E508", {"start": v(-557.24, 264.73) * mm, "mid": v(-558.37, 264.5) * mm, "end": v(-559.46, 264.12) * mm});
            skArc(sketch, "E509", {"start": v(-559.46, 264.12) * mm, "mid": v(-560.28, 263.7) * mm, "end": v(-561.05, 263.2) * mm});
            skArc(sketch, "E510", {"start": v(-561.05, 263.2) * mm, "mid": v(-561.76, 262.61) * mm, "end": v(-562.4, 261.95) * mm});
            skArc(sketch, "E511", {"start": v(-562.4, 261.95) * mm, "mid": v(-562.95, 261.21) * mm, "end": v(-563.42, 260.42) * mm});
            skArc(sketch, "E512", {"start": v(-563.42, 260.42) * mm, "mid": v(-563.82, 259.48) * mm, "end": v(-564.12, 258.5) * mm});
            skLineSegment(sketch, "E513", {"start": v(-564.12, 258.5) * mm, "end": v(-564.6, 256.52) * mm});
            skArc(sketch, "E514", {"start": v(-564.6, 256.52) * mm, "mid": v(-565.02, 255.48) * mm, "end": v(-565.58, 254.5) * mm});
            skArc(sketch, "E515", {"start": v(-565.58, 254.5) * mm, "mid": v(-566.71, 253.7) * mm, "end": v(-568.06, 253.38) * mm});
            skArc(sketch, "E516", {"start": v(-568.06, 253.38) * mm, "mid": v(-568.72, 253.4) * mm, "end": v(-569.38, 253.52) * mm});
            skArc(sketch, "E517", {"start": v(-569.38, 253.52) * mm, "mid": v(-570.03, 253.77) * mm, "end": v(-570.62, 254.14) * mm});
            skArc(sketch, "E518", {"start": v(-570.62, 254.14) * mm, "mid": v(-571.48, 254.97) * mm, "end": v(-572.1, 256) * mm});
            skLineSegment(sketch, "E519", {"start": v(-572.1, 256) * mm, "end": v(-573.27, 255.4) * mm});
            skArc(sketch, "E520", {"start": v(-573.27, 255.4) * mm, "mid": v(-572.67, 254) * mm, "end": v(-571.92, 252.66) * mm});
            skArc(sketch, "E521", {"start": v(-571.92, 252.66) * mm, "mid": v(-571.3, 251.84) * mm, "end": v(-570.6, 251.08) * mm});
            skArc(sketch, "E522", {"start": v(-570.6, 251.08) * mm, "mid": v(-568.98, 249.8) * mm, "end": v(-567.14, 248.88) * mm});
            skArc(sketch, "E523", {"start": v(-567.14, 248.88) * mm, "mid": v(-568.28, 247.34) * mm, "end": v(-569.6, 245.96) * mm});
            skArc(sketch, "E524", {"start": v(-569.6, 245.96) * mm, "mid": v(-570.98, 244.88) * mm, "end": v(-572.47, 243.95) * mm});
            skArc(sketch, "E525", {"start": v(-572.47, 243.95) * mm, "mid": v(-573.42, 243.47) * mm, "end": v(-574.41, 243.05) * mm});
            skArc(sketch, "E526", {"start": v(-574.41, 243.05) * mm, "mid": v(-577.1, 242.85) * mm, "end": v(-579.63, 243.79) * mm});
            skLineSegment(sketch, "E527", {"start": v(-579.64, 243.79) * mm, "end": v(-582.95, 245.45) * mm});
            skLineSegment(sketch, "E528", {"start": v(-582.95, 245.45) * mm, "end": v(-583.49, 244.97) * mm});
            skLineSegment(sketch, "E529", {"start": v(-583.49, 244.97) * mm, "end": v(-582.3, 241.71) * mm});
            skArc(sketch, "E530", {"start": v(-582.3, 241.71) * mm, "mid": v(-581.77, 241.14) * mm, "end": v(-581.19, 240.6) * mm});
            skArc(sketch, "E531", {"start": v(-581.19, 240.6) * mm, "mid": v(-580.57, 240.12) * mm, "end": v(-579.91, 239.7) * mm});
            skArc(sketch, "E532", {"start": v(-579.91, 239.7) * mm, "mid": v(-578.5, 238.99) * mm, "end": v(-577, 238.5) * mm});
            skArc(sketch, "E533", {"start": v(-577, 238.5) * mm, "mid": v(-575.45, 238.27) * mm, "end": v(-573.88, 238.28) * mm});
            skArc(sketch, "E534", {"start": v(-573.88, 238.28) * mm, "mid": v(-572.49, 238.62) * mm, "end": v(-571.09, 238.92) * mm});
            skLineSegment(sketch, "E535", {"start": v(-571.09, 238.92) * mm, "end": v(-570.42, 239) * mm});
            skArc(sketch, "E536", {"start": v(-570.42, 239) * mm, "mid": v(-570.3, 239) * mm, "end": v(-570.24, 238.9) * mm});
            skArc(sketch, "E537", {"start": v(-570.24, 238.9) * mm, "mid": v(-570.7, 238.57) * mm, "end": v(-571.2, 238.3) * mm});
            skLineSegment(sketch, "E538", {"start": v(-571.2, 238.3) * mm, "end": v(-572.79, 237.58) * mm});
            skArc(sketch, "E539", {"start": v(-572.79, 237.58) * mm, "mid": v(-574.6, 237.04) * mm, "end": v(-576.47, 236.76) * mm});
            skLineSegment(sketch, "E540", {"start": v(-576.47, 236.76) * mm, "end": v(-576.65, 236.11) * mm});
            skArc(sketch, "E541", {"start": v(-576.65, 236.11) * mm, "mid": v(-574.1, 234.44) * mm, "end": v(-571.11, 233.76) * mm});
            skArc(sketch, "E542", {"start": v(-571.11, 233.76) * mm, "mid": v(-569.8, 233.8) * mm, "end": v(-568.5, 234.05) * mm});
            skArc(sketch, "E543", {"start": v(-568.5, 234.05) * mm, "mid": v(-568.38, 233.9) * mm, "end": v(-568.47, 233.71) * mm});
            skArc(sketch, "E544", {"start": v(-568.47, 233.71) * mm, "mid": v(-570, 230.7) * mm, "end": v(-571.4, 227.62) * mm});
            skArc(sketch, "E545", {"start": v(-571.4, 227.62) * mm, "mid": v(-572.7, 224.5) * mm, "end": v(-573.9, 221.33) * mm});
            skArc(sketch, "E546", {"start": v(-573.9, 221.33) * mm, "mid": v(-574.52, 219.61) * mm, "end": v(-575.23, 217.92) * mm});
            skArc(sketch, "E547", {"start": v(-575.23, 217.92) * mm, "mid": v(-575.93, 216.25) * mm, "end": v(-576.58, 214.56) * mm});
            skArc(sketch, "E548", {"start": v(-576.58, 214.56) * mm, "mid": v(-577.26, 212.56) * mm, "end": v(-577.87, 210.54) * mm});
            skArc(sketch, "E549", {"start": v(-577.87, 210.54) * mm, "mid": v(-577.92, 210.27) * mm, "end": v(-578.1, 210.05) * mm});
            skLineSegment(sketch, "E550", {"start": v(-578.1, 210.05) * mm, "end": v(-579.46, 209.36) * mm});
            skArc(sketch, "E551", {"start": v(-579.46, 209.36) * mm, "mid": v(-580.76, 208.47) * mm, "end": v(-582, 207.48) * mm});
            skLineSegment(sketch, "E552", {"start": v(-582, 207.48) * mm, "end": v(-583.54, 206.67) * mm});
            skLineSegment(sketch, "E553", {"start": v(-583.54, 206.67) * mm, "end": v(-583.77, 206.48) * mm});
            skArc(sketch, "E554", {"start": v(-583.77, 206.48) * mm, "mid": v(-584.25, 205.53) * mm, "end": v(-584, 204.5) * mm});
            skLineSegment(sketch, "E555", {"start": v(-584, 204.5) * mm, "end": v(-583.7, 204.05) * mm});
            skArc(sketch, "E556", {"start": v(-583.7, 204.05) * mm, "mid": v(-582.55, 204.34) * mm, "end": v(-581.42, 204.76) * mm});
            skLineSegment(sketch, "E557", {"start": v(-581.42, 204.76) * mm, "end": v(-579.39, 205.88) * mm});
            skArc(sketch, "E558", {"start": v(-579.39, 205.88) * mm, "mid": v(-578.28, 206.01) * mm, "end": v(-577.26, 205.6) * mm});
            skArc(sketch, "E559", {"start": v(-577.26, 205.6) * mm, "mid": v(-576.97, 205.24) * mm, "end": v(-576.8, 204.82) * mm});
            skLineSegment(sketch, "E560", {"start": v(-576.8, 204.82) * mm, "end": v(-576.5, 204.25) * mm});
            skArc(sketch, "E561", {"start": v(-576.5, 204.25) * mm, "mid": v(-575.72, 203.56) * mm, "end": v(-574.72, 203.3) * mm});
            skArc(sketch, "E562", {"start": v(-574.72, 203.3) * mm, "mid": v(-573.91, 203.32) * mm, "end": v(-573.17, 203.65) * mm});
            skLineSegment(sketch, "E563", {"start": v(-573.17, 203.65) * mm, "end": v(-572.5, 204.14) * mm});
            skLineSegment(sketch, "E564", {"start": v(-572.5, 204.14) * mm, "end": v(-572.5, 204.21) * mm});
            skLineSegment(sketch, "E565", {"start": v(-572.5, 204.21) * mm, "end": v(-573.1, 204.8) * mm});
            skArc(sketch, "E566", {"start": v(-573.1, 204.8) * mm, "mid": v(-573.54, 205.27) * mm, "end": v(-573.88, 205.81) * mm});
            skArc(sketch, "E567", {"start": v(-573.88, 205.81) * mm, "mid": v(-574.26, 207.03) * mm, "end": v(-574.22, 208.31) * mm});
            skArc(sketch, "E568", {"start": v(-574.22, 208.31) * mm, "mid": v(-574, 208.91) * mm, "end": v(-573.75, 209.5) * mm});
            skLineSegment(sketch, "E569", {"start": v(-573.75, 209.5) * mm, "end": v(-572.34, 213.16) * mm});
            skArc(sketch, "E570", {"start": v(-572.34, 213.16) * mm, "mid": v(-571.06, 215.54) * mm, "end": v(-569.41, 217.69) * mm});
            skArc(sketch, "E571", {"start": v(-569.41, 217.69) * mm, "mid": v(-567.27, 220.63) * mm, "end": v(-565.25, 223.66) * mm});
            skArc(sketch, "E572", {"start": v(-565.25, 223.66) * mm, "mid": v(-562.98, 227.43) * mm, "end": v(-560.9, 231.32) * mm});
            skArc(sketch, "E573", {"start": v(-560.9, 231.32) * mm, "mid": v(-560.5, 231.49) * mm, "end": v(-560.16, 231.22) * mm});
            skArc(sketch, "E574", {"start": v(-560.16, 231.22) * mm, "mid": v(-559.82, 230.08) * mm, "end": v(-559.3, 229) * mm});
            skArc(sketch, "E575", {"start": v(-559.3, 229) * mm, "mid": v(-558.72, 227.96) * mm, "end": v(-558.19, 226.88) * mm});
            skArc(sketch, "E576", {"start": v(-558.19, 226.88) * mm, "mid": v(-557.52, 224.64) * mm, "end": v(-557.16, 222.34) * mm});
            skArc(sketch, "E577", {"start": v(-557.16, 222.34) * mm, "mid": v(-557, 220.14) * mm, "end": v(-557.07, 217.94) * mm});
            skArc(sketch, "E578", {"start": v(-557.07, 217.94) * mm, "mid": v(-557.31, 216.28) * mm, "end": v(-557.78, 214.67) * mm});
            skArc(sketch, "E579", {"start": v(-557.78, 214.67) * mm, "mid": v(-558.44, 213.28) * mm, "end": v(-559.3, 211.99) * mm});
            skArc(sketch, "E580", {"start": v(-559.3, 211.99) * mm, "mid": v(-559.54, 210.45) * mm, "end": v(-559.43, 208.89) * mm});
            skArc(sketch, "E581", {"start": v(-559.43, 208.89) * mm, "mid": v(-559.1, 207.66) * mm, "end": v(-558.55, 206.51) * mm});
            skArc(sketch, "E582", {"start": v(-558.55, 206.51) * mm, "mid": v(-557.72, 205.4) * mm, "end": v(-556.7, 204.48) * mm});
            skArc(sketch, "E583", {"start": v(-556.7, 204.48) * mm, "mid": v(-555.14, 203.6) * mm, "end": v(-553.4, 203.14) * mm});
            skArc(sketch, "E584", {"start": v(-553.4, 203.14) * mm, "mid": v(-551.68, 203.02) * mm, "end": v(-549.96, 203.03) * mm});
            skArc(sketch, "E585", {"start": v(-549.96, 203.03) * mm, "mid": v(-547.8, 203.1) * mm, "end": v(-545.67, 203.3) * mm});
            skLineSegment(sketch, "E586", {"start": v(-545.67, 203.3) * mm, "end": v(-544.97, 203.63) * mm});
            skLineSegment(sketch, "E587", {"start": v(-544.97, 203.63) * mm, "end": v(-543.46, 204.81) * mm});
            skArc(sketch, "E588", {"start": v(-543.46, 204.81) * mm, "mid": v(-541, 206.92) * mm, "end": v(-538.66, 209.17) * mm});
            skArc(sketch, "E589", {"start": v(-538.66, 209.17) * mm, "mid": v(-536.08, 211.98) * mm, "end": v(-533.69, 214.96) * mm});
            skArc(sketch, "E590", {"start": v(-533.69, 214.96) * mm, "mid": v(-532.41, 217.16) * mm, "end": v(-530.87, 219.18) * mm});
            skArc(sketch, "E591", {"start": v(-530.87, 219.18) * mm, "mid": v(-529.09, 220.99) * mm, "end": v(-527.1, 222.56) * mm});
            skArc(sketch, "E592", {"start": v(-527.1, 222.56) * mm, "mid": v(-526.49, 223.13) * mm, "end": v(-525.68, 223.36) * mm});
            skArc(sketch, "E593", {"start": v(-525.68, 223.36) * mm, "mid": v(-524.83, 223.15) * mm, "end": v(-524.1, 222.66) * mm});
            skLineSegment(sketch, "E594", {"start": v(-524.1, 222.66) * mm, "end": v(-523.34, 222.2) * mm});
            skArc(sketch, "E595", {"start": v(-523.34, 222.2) * mm, "mid": v(-522.33, 220.77) * mm, "end": v(-521.17, 219.45) * mm});
            skArc(sketch, "E596", {"start": v(-521.17, 219.45) * mm, "mid": v(-519.9, 218.28) * mm, "end": v(-518.54, 217.24) * mm});
            skArc(sketch, "E597", {"start": v(-518.54, 217.24) * mm, "mid": v(-515.82, 215.69) * mm, "end": v(-512.88, 214.62) * mm});
            skArc(sketch, "E598", {"start": v(-512.88, 214.62) * mm, "mid": v(-511.5, 214.36) * mm, "end": v(-510.17, 213.88) * mm});
            skArc(sketch, "E599", {"start": v(-510.17, 213.88) * mm, "mid": v(-508.94, 213.18) * mm, "end": v(-507.84, 212.3) * mm});
            skArc(sketch, "E600", {"start": v(-507.84, 212.3) * mm, "mid": v(-507.72, 211) * mm, "end": v(-507.91, 209.73) * mm});
            skArc(sketch, "E601", {"start": v(-507.91, 209.73) * mm, "mid": v(-507.83, 208.91) * mm, "end": v(-507.43, 208.2) * mm});
            skArc(sketch, "E602", {"start": v(-507.43, 208.2) * mm, "mid": v(-506.54, 207.56) * mm, "end": v(-505.44, 207.46) * mm});
            skLineSegment(sketch, "E603", {"start": v(-505.44, 207.46) * mm, "end": v(-503.57, 208.16) * mm});
            skArc(sketch, "E604", {"start": v(-503.57, 208.16) * mm, "mid": v(-502.38, 208.25) * mm, "end": v(-501.22, 207.98) * mm});
            skLineSegment(sketch, "E605", {"start": v(-501.22, 207.98) * mm, "end": v(-500.18, 207.37) * mm});
            skArc(sketch, "E606", {"start": v(-500.18, 207.37) * mm, "mid": v(-499.56, 207.24) * mm, "end": v(-498.93, 207.3) * mm});
            skArc(sketch, "E607", {"start": v(-498.93, 207.3) * mm, "mid": v(-498.27, 207.4) * mm, "end": v(-497.6, 207.42) * mm});
            skArc(sketch, "E608", {"start": v(-497.6, 207.42) * mm, "mid": v(-496.33, 207.24) * mm, "end": v(-495.09, 206.92) * mm});
            skLineSegment(sketch, "E609", {"start": v(-495.09, 206.92) * mm, "end": v(-494.58, 207.33) * mm});
            skArc(sketch, "E610", {"start": v(-494.58, 207.33) * mm, "mid": v(-494.14, 208.1) * mm, "end": v(-494.12, 208.97) * mm});
            skArc(sketch, "E611", {"start": v(-494.12, 208.97) * mm, "mid": v(-494.24, 209.31) * mm, "end": v(-494.43, 209.63) * mm});
            skArc(sketch, "E612", {"start": v(-494.43, 209.63) * mm, "mid": v(-494.65, 209.87) * mm, "end": v(-494.91, 210.08) * mm});
            skArc(sketch, "E613", {"start": v(-494.91, 210.08) * mm, "mid": v(-495.26, 210.26) * mm, "end": v(-495.64, 210.37) * mm});
            skLineSegment(sketch, "E614", {"start": v(-495.64, 210.37) * mm, "end": v(-496.93, 210.7) * mm});
            skArc(sketch, "E615", {"start": v(-496.93, 210.7) * mm, "mid": v(-497.6, 211) * mm, "end": v(-498.23, 211.39) * mm});
            skArc(sketch, "E616", {"start": v(-498.23, 211.39) * mm, "mid": v(-499.06, 212.2) * mm, "end": v(-500.01, 212.9) * mm});
            skArc(sketch, "E617", {"start": v(-500.01, 212.9) * mm, "mid": v(-501.05, 213.43) * mm, "end": v(-502.16, 213.8) * mm});
            skLineSegment(sketch, "E618", {"start": v(-502.16, 213.8) * mm, "end": v(-504.45, 215.13) * mm});
            skLineSegment(sketch, "E619", {"start": v(-504.45, 215.13) * mm, "end": v(-510.37, 220.65) * mm});
            skArc(sketch, "E620", {"start": v(-510.37, 220.65) * mm, "mid": v(-512.45, 222.57) * mm, "end": v(-514.43, 224.6) * mm});
            skArc(sketch, "E621", {"start": v(-514.43, 224.6) * mm, "mid": v(-516.94, 227.5) * mm, "end": v(-519.25, 230.56) * mm});
            skArc(sketch, "E622", {"start": v(-519.25, 230.56) * mm, "mid": v(-519.99, 231.3) * mm, "end": v(-520.86, 231.89) * mm});
            skArc(sketch, "E623", {"start": v(-520.86, 231.89) * mm, "mid": v(-522.76, 232.54) * mm, "end": v(-524.77, 232.63) * mm});
            skArc(sketch, "E624", {"start": v(-524.77, 232.63) * mm, "mid": v(-526.09, 232.34) * mm, "end": v(-527.34, 231.84) * mm});
            skArc(sketch, "E625", {"start": v(-527.34, 231.84) * mm, "mid": v(-532.17, 229.45) * mm, "end": v(-536.84, 226.76) * mm});
            skArc(sketch, "E626", {"start": v(-536.84, 226.76) * mm, "mid": v(-541.97, 223.28) * mm, "end": v(-546.8, 219.4) * mm});
            skArc(sketch, "E627", {"start": v(-546.8, 219.4) * mm, "mid": v(-547.04, 219.36) * mm, "end": v(-547.26, 219.46) * mm});
            skArc(sketch, "E628", {"start": v(-547.26, 219.46) * mm, "mid": v(-547.81, 220.25) * mm, "end": v(-548.04, 221.19) * mm});
            skLineSegment(sketch, "E629", {"start": v(-548.04, 221.19) * mm, "end": v(-548.19, 223.23) * mm});
            skArc(sketch, "E630", {"start": v(-548.19, 223.23) * mm, "mid": v(-548.3, 225.17) * mm, "end": v(-548.2, 227.1) * mm});
            skLineSegment(sketch, "E631", {"start": v(-548.2, 227.1) * mm, "end": v(-547.73, 227.99) * mm});
            skArc(sketch, "E632", {"start": v(-547.73, 227.99) * mm, "mid": v(-547.43, 228.39) * mm, "end": v(-547.08, 228.74) * mm});
            skLineSegment(sketch, "E633", {"start": v(-547.08, 228.74) * mm, "end": v(-546.04, 229.51) * mm});
            skArc(sketch, "E634", {"start": v(-546.04, 229.51) * mm, "mid": v(-545.13, 230.31) * mm, "end": v(-544.36, 231.25) * mm});
            skArc(sketch, "E635", {"start": v(-544.36, 231.25) * mm, "mid": v(-543.64, 232.63) * mm, "end": v(-543.16, 234.1) * mm});
            skArc(sketch, "E636", {"start": v(-543.16, 234.1) * mm, "mid": v(-542.98, 234.41) * mm, "end": v(-542.75, 234.7) * mm});
            skLineSegment(sketch, "E637", {"start": v(-542.75, 234.7) * mm, "end": v(-542.95, 235.81) * mm});
            skArc(sketch, "E638", {"start": v(-542.95, 235.81) * mm, "mid": v(-543.38, 235.84) * mm, "end": v(-543.8, 235.94) * mm});
            skArc(sketch, "E639", {"start": v(-543.8, 235.94) * mm, "mid": v(-544.46, 236.67) * mm, "end": v(-545.16, 237.36) * mm});
            skArc(sketch, "E640", {"start": v(-545.16, 237.36) * mm, "mid": v(-546.18, 238.09) * mm, "end": v(-547.31, 238.64) * mm});
            skArc(sketch, "E641", {"start": v(-547.31, 238.64) * mm, "mid": v(-548.52, 239) * mm, "end": v(-549.77, 239.14) * mm});
            skArc(sketch, "E642", {"start": v(-549.77, 239.14) * mm, "mid": v(-550.41, 239.57) * mm, "end": v(-551, 240.08) * mm});
            skArc(sketch, "E643", {"start": v(-551, 240.08) * mm, "mid": v(-551.8, 241.1) * mm, "end": v(-552.18, 242.35) * mm});
            skArc(sketch, "E644", {"start": v(-552.18, 242.35) * mm, "mid": v(-552.06, 243.4) * mm, "end": v(-551.58, 244.33) * mm});
            skArc(sketch, "E645", {"start": v(-551.58, 244.33) * mm, "mid": v(-551.04, 244.33) * mm, "end": v(-550.54, 244.12) * mm});
            skArc(sketch, "E646", {"start": v(-550.54, 244.12) * mm, "mid": v(-549.37, 243.87) * mm, "end": v(-548.25, 244.28) * mm});
            skArc(sketch, "E647", {"start": v(-548.25, 244.28) * mm, "mid": v(-547.95, 244.53) * mm, "end": v(-547.7, 244.83) * mm});
            skArc(sketch, "E648", {"start": v(-547.7, 244.83) * mm, "mid": v(-547.5, 245.17) * mm, "end": v(-547.36, 245.53) * mm});
            skLineSegment(sketch, "E649", {"start": v(-547.36, 245.53) * mm, "end": v(-546.08, 248.76) * mm});
            skArc(sketch, "E650", {"start": v(-546.08, 248.76) * mm, "mid": v(-545.77, 248.8) * mm, "end": v(-545.5, 249) * mm});
            skArc(sketch, "E651", {"start": v(-545.5, 249) * mm, "mid": v(-545.3, 249.47) * mm, "end": v(-545.46, 249.97) * mm});
            skArc(sketch, "E652", {"start": v(-545.46, 249.97) * mm, "mid": v(-546.02, 250.92) * mm, "end": v(-546.31, 251.99) * mm});
            skLineSegment(sketch, "E653", {"start": v(-546.31, 251.99) * mm, "end": v(-545.48, 252.93) * mm});
            skArc(sketch, "E654", {"start": v(-280.09, 297.1) * mm, "mid": v(-266.57, 294.63) * mm, "end": v(-253.05, 297.1) * mm});
            skArc(sketch, "E655", {"start": v(-253.05, 222.36) * mm, "mid": v(-266.57, 224.84) * mm, "end": v(-280.09, 222.36) * mm});
            skCircle(sketch, "E656", {"center": v(-266.57, 259.73) * mm, "radius": 22.42 * mm});
            skArc(sketch, "E657", {"start": v(-294.82, 235.4) * mm, "mid": v(-291.86, 259.73) * mm, "end": v(-294.82, 284.06) * mm});
            skArc(sketch, "E658", {"start": v(-294.82, 235.4) * mm, "mid": v(-291.4, 224.43) * mm, "end": v(-280.09, 222.36) * mm});
            skCircle(sketch, "E659", {"center": v(-284.03, 232.75) * mm, "radius": 5.56 * mm});
            skCircle(sketch, "E660", {"center": v(-284.03, 286.72) * mm, "radius": 5.56 * mm});
            skArc(sketch, "E661", {"start": v(-280.09, 297.1) * mm, "mid": v(-291.4, 295.04) * mm, "end": v(-294.82, 284.06) * mm});
            skArc(sketch, "E662", {"start": v(-238.32, 284.06) * mm, "mid": v(-241.27, 259.73) * mm, "end": v(-238.32, 235.4) * mm});
            skArc(sketch, "E663", {"start": v(-253.05, 222.36) * mm, "mid": v(-241.74, 224.43) * mm, "end": v(-238.32, 235.4) * mm});
            skCircle(sketch, "E664", {"center": v(-249.1, 232.75) * mm, "radius": 5.56 * mm});
            skArc(sketch, "E665", {"start": v(-238.32, 284.06) * mm, "mid": v(-241.74, 295.04) * mm, "end": v(-253.05, 297.1) * mm});
            skCircle(sketch, "E666", {"center": v(-249.1, 286.72) * mm, "radius": 5.56 * mm});
            skCircle(sketch, "E667", {"center": v(-195.77, 263.23) * mm, "radius": 4.76 * mm});
            skCircle(sketch, "E668", {"center": v(-151.31, 218.78) * mm, "radius": 4.76 * mm});
            skCircle(sketch, "E669", {"center": v(-106.86, 263.23) * mm, "radius": 4.76 * mm});
            skArc(sketch, "E670", {"start": v(-140.55, 216) * mm, "mid": v(-127.3, 239.2) * mm, "end": v(-104.08, 252.47) * mm});
            skArc(sketch, "E671", {"start": v(-104.08, 252.47) * mm, "mid": v(-95.75, 263.23) * mm, "end": v(-104.08, 273.99) * mm});
            skArc(sketch, "E672", {"start": v(-104.08, 273.99) * mm, "mid": v(-127.3, 287.25) * mm, "end": v(-140.55, 310.46) * mm});
            skArc(sketch, "E673", {"start": v(-140.55, 310.46) * mm, "mid": v(-151.31, 318.8) * mm, "end": v(-162.07, 310.46) * mm});
            skArc(sketch, "E674", {"start": v(-162.07, 310.46) * mm, "mid": v(-175.34, 287.25) * mm, "end": v(-198.55, 273.99) * mm});
            skArc(sketch, "E675", {"start": v(-198.55, 273.99) * mm, "mid": v(-206.88, 263.23) * mm, "end": v(-198.55, 252.47) * mm});
            skArc(sketch, "E676", {"start": v(-198.55, 252.47) * mm, "mid": v(-175.34, 239.2) * mm, "end": v(-162.07, 216) * mm});
            skArc(sketch, "E677", {"start": v(-162.07, 216) * mm, "mid": v(-151.31, 207.67) * mm, "end": v(-140.55, 216) * mm});
            skCircle(sketch, "E678", {"center": v(-151.31, 307.68) * mm, "radius": 4.76 * mm});
            skCircle(sketch, "E679", {"center": v(-151.31, 263.23) * mm, "radius": 22.23 * mm});
            skLineSegment(sketch, "E680", {"start": v(-450.6, 304.37) * mm, "end": v(-379.13, 304.37) * mm});
            skLineSegment(sketch, "E681", {"start": v(-419.71, 331.4) * mm, "end": v(-435.88, 323.15) * mm});
            skLineSegment(sketch, "E682", {"start": v(-441.92, 320.1) * mm, "end": v(-450.6, 304.52) * mm});
            skLineSegment(sketch, "E683", {"start": v(-450.6, 304.52) * mm, "end": v(-450.6, 304.37) * mm});
            skLineSegment(sketch, "E684", {"start": v(-435.88, 323.15) * mm, "end": v(-441.92, 320.1) * mm});
            skLineSegment(sketch, "E685", {"start": v(-379.13, 304.45) * mm, "end": v(-388, 320.13) * mm});
            skCircle(sketch, "E686", {"center": v(-415.04, 319.53) * mm, "radius": 5.08 * mm});
            skArc(sketch, "E687", {"start": v(-388, 320.13) * mm, "mid": v(-399.11, 325.8) * mm, "end": v(-410.24, 331.43) * mm});
            skLineSegment(sketch, "E688", {"start": v(-433.84, 319.48) * mm, "end": v(-434, 319.48) * mm});
            skArc(sketch, "E689", {"start": v(-410.24, 331.43) * mm, "mid": v(-414.98, 332.33) * mm, "end": v(-419.71, 331.4) * mm});
            skLineSegment(sketch, "E690", {"start": v(-395.98, 319.53) * mm, "end": v(-395.82, 319.53) * mm});
            skLineSegment(sketch, "E691", {"start": v(-379.13, 304.37) * mm, "end": v(-379.13, 304.45) * mm});
            skCircle(sketch, "E692", {"center": v(575.83, 281.74) * mm, "radius": 9.56 * mm});
            skArc(sketch, "E693", {"start": v(538.55, 302.04) * mm, "mid": v(631.14, 304.98) * mm, "end": v(720.89, 327.88) * mm});
            skLineSegment(sketch, "E694", {"start": v(746.63, 115.98) * mm, "end": v(518.03, 115.98) * mm});
            skLineSegment(sketch, "E695", {"start": v(518.03, 115.98) * mm, "end": v(518.03, 283.04) * mm});
            skArc(sketch, "E696", {"start": v(538.55, 302.04) * mm, "mid": v(524.14, 297.03) * mm, "end": v(518.03, 283.04) * mm});
            skCircle(sketch, "E697", {"center": v(537.08, 283.04) * mm, "radius": 9.56 * mm});
            skLineSegment(sketch, "E698", {"start": v(746.63, 115.98) * mm, "end": v(746.63, 310.05) * mm});
            skArc(sketch, "E699", {"start": v(746.63, 310.05) * mm, "mid": v(738.43, 325.7) * mm, "end": v(720.89, 327.88) * mm});
            skCircle(sketch, "E700", {"center": v(690.72, 298.02) * mm, "radius": 9.56 * mm});
            skCircle(sketch, "E701", {"center": v(652.95, 289.25) * mm, "radius": 9.56 * mm});
            skCircle(sketch, "E702", {"center": v(614.55, 283.81) * mm, "radius": 9.56 * mm});
            skCircle(sketch, "E703", {"center": v(727.59, 310.05) * mm, "radius": 9.56 * mm});
            skLineSegment(sketch, "E704", {"start": v(-1569.03, 406.5) * mm, "end": v(-1567.44, 405.6) * mm});
            skLineSegment(sketch, "E705", {"start": v(-1556.22, 153.51) * mm, "end": v(-1656.42, 153.51) * mm});
            skLineSegment(sketch, "E706", {"start": v(-1656.5, 177.08) * mm, "end": v(-1656.5, 385.72) * mm});
            skLineSegment(sketch, "E707", {"start": v(-1656.42, 153.51) * mm, "end": v(-1656.42, 175.07) * mm});
            skLineSegment(sketch, "E708", {"start": v(-1656.42, 175.07) * mm, "end": v(-1656.5, 177.08) * mm});
            skLineSegment(sketch, "E709", {"start": v(-1633.19, 409.04) * mm, "end": v(-1579.62, 409.04) * mm});
            skLineSegment(sketch, "E710", {"start": v(-1617.31, 340.26) * mm, "end": v(-1615.22, 339.4) * mm});
            skLineSegment(sketch, "E711", {"start": v(-1615.22, 388.09) * mm, "end": v(-1617.31, 387.22) * mm});
            skLineSegment(sketch, "E712", {"start": v(-1628.8, 376.7) * mm, "end": v(-1629.84, 374.7) * mm});
            skLineSegment(sketch, "E713", {"start": v(-1628.8, 350.79) * mm, "end": v(-1627.58, 348.88) * mm});
            skLineSegment(sketch, "E714", {"start": v(-1637.1, 333.14) * mm, "end": v(-1636.62, 332.78) * mm});
            skLineSegment(sketch, "E715", {"start": v(-1634.44, 332.72) * mm, "end": v(-1633.97, 333.04) * mm});
            skLineSegment(sketch, "E716", {"start": v(-1635.48, 335.77) * mm, "end": v(-1635.48, 332.47) * mm});
            skLineSegment(sketch, "E717", {"start": v(-1636.07, 332.55) * mm, "end": v(-1635.48, 332.47) * mm});
            skLineSegment(sketch, "E718", {"start": v(-1636.62, 332.78) * mm, "end": v(-1636.07, 332.55) * mm});
            skLineSegment(sketch, "E719", {"start": v(-1634.97, 332.53) * mm, "end": v(-1634.44, 332.72) * mm});
            skLineSegment(sketch, "E720", {"start": v(-1635.48, 332.47) * mm, "end": v(-1634.97, 332.53) * mm});
            skLineSegment(sketch, "E721", {"start": v(-1633.7, 336.2) * mm, "end": v(-1634.11, 336.6) * mm});
            skLineSegment(sketch, "E722", {"start": v(-1633.97, 333.04) * mm, "end": v(-1633.57, 333.47) * mm});
            skLineSegment(sketch, "E723", {"start": v(-1636.25, 336.92) * mm, "end": v(-1636.75, 336.65) * mm});
            skLineSegment(sketch, "E724", {"start": v(-1637.45, 333.61) * mm, "end": v(-1637.1, 333.14) * mm});
            skLineSegment(sketch, "E725", {"start": v(-1637.69, 334.14) * mm, "end": v(-1637.45, 333.61) * mm});
            skLineSegment(sketch, "E726", {"start": v(-1637.78, 334.7) * mm, "end": v(-1637.69, 334.14) * mm});
            skLineSegment(sketch, "E727", {"start": v(-1637.72, 335.28) * mm, "end": v(-1637.78, 334.7) * mm});
            skLineSegment(sketch, "E728", {"start": v(-1637.52, 335.82) * mm, "end": v(-1637.72, 335.28) * mm});
            skLineSegment(sketch, "E729", {"start": v(-1637.19, 336.29) * mm, "end": v(-1637.52, 335.82) * mm});
            skLineSegment(sketch, "E730", {"start": v(-1636.75, 336.65) * mm, "end": v(-1637.19, 336.29) * mm});
            skLineSegment(sketch, "E731", {"start": v(-1635.7, 337.04) * mm, "end": v(-1636.25, 336.92) * mm});
            skLineSegment(sketch, "E732", {"start": v(-1635.14, 337.03) * mm, "end": v(-1635.7, 337.04) * mm});
            skLineSegment(sketch, "E733", {"start": v(-1634.6, 336.88) * mm, "end": v(-1635.14, 337.03) * mm});
            skLineSegment(sketch, "E734", {"start": v(-1634.11, 336.6) * mm, "end": v(-1634.6, 336.88) * mm});
            skLineSegment(sketch, "E735", {"start": v(-1630.7, 354.88) * mm, "end": v(-1629.84, 352.8) * mm});
            skLineSegment(sketch, "E736", {"start": v(-1633.39, 335.71) * mm, "end": v(-1633.7, 336.2) * mm});
            skLineSegment(sketch, "E737", {"start": v(-1633.2, 335.15) * mm, "end": v(-1633.39, 335.71) * mm});
            skLineSegment(sketch, "E738", {"start": v(-1633.18, 334.57) * mm, "end": v(-1633.2, 335.15) * mm});
            skLineSegment(sketch, "E739", {"start": v(-1633.3, 334) * mm, "end": v(-1633.18, 334.57) * mm});
            skLineSegment(sketch, "E740", {"start": v(-1633.57, 333.47) * mm, "end": v(-1633.3, 334) * mm});
            skLineSegment(sketch, "E741", {"start": v(-1629.84, 352.8) * mm, "end": v(-1628.8, 350.79) * mm});
            skLineSegment(sketch, "E742", {"start": v(-1631.39, 357.04) * mm, "end": v(-1630.7, 354.88) * mm});
            skLineSegment(sketch, "E743", {"start": v(-1630.7, 372.6) * mm, "end": v(-1631.39, 370.45) * mm});
            skLineSegment(sketch, "E744", {"start": v(-1631.88, 359.24) * mm, "end": v(-1631.39, 357.04) * mm});
            skLineSegment(sketch, "E745", {"start": v(-1632.17, 361.49) * mm, "end": v(-1631.88, 359.24) * mm});
            skLineSegment(sketch, "E746", {"start": v(-1632.27, 363.74) * mm, "end": v(-1632.17, 361.49) * mm});
            skLineSegment(sketch, "E747", {"start": v(-1632.17, 366) * mm, "end": v(-1632.27, 363.74) * mm});
            skLineSegment(sketch, "E748", {"start": v(-1631.88, 368.24) * mm, "end": v(-1632.17, 366) * mm});
            skLineSegment(sketch, "E749", {"start": v(-1631.39, 370.45) * mm, "end": v(-1631.88, 368.24) * mm});
            skLineSegment(sketch, "E750", {"start": v(-1629.84, 374.7) * mm, "end": v(-1630.7, 372.6) * mm});
            skLineSegment(sketch, "E751", {"start": v(-1623.01, 343.9) * mm, "end": v(-1621.22, 342.52) * mm});
            skLineSegment(sketch, "E752", {"start": v(-1626.2, 347.1) * mm, "end": v(-1624.68, 345.42) * mm});
            skLineSegment(sketch, "E753", {"start": v(-1627.58, 348.88) * mm, "end": v(-1626.2, 347.1) * mm});
            skLineSegment(sketch, "E754", {"start": v(-1624.68, 345.42) * mm, "end": v(-1623.01, 343.9) * mm});
            skLineSegment(sketch, "E755", {"start": v(-1619.32, 341.3) * mm, "end": v(-1617.31, 340.26) * mm});
            skLineSegment(sketch, "E756", {"start": v(-1621.22, 342.52) * mm, "end": v(-1619.32, 341.3) * mm});
            skLineSegment(sketch, "E757", {"start": v(-1640.4, 407.9) * mm, "end": v(-1638.63, 408.4) * mm});
            skLineSegment(sketch, "E758", {"start": v(-1652.05, 399.42) * mm, "end": v(-1650.92, 400.86) * mm});
            skLineSegment(sketch, "E759", {"start": v(-1653.96, 396.3) * mm, "end": v(-1653.07, 397.9) * mm});
            skLineSegment(sketch, "E760", {"start": v(-1654.73, 394.64) * mm, "end": v(-1653.96, 396.3) * mm});
            skLineSegment(sketch, "E761", {"start": v(-1655.37, 392.92) * mm, "end": v(-1654.73, 394.64) * mm});
            skLineSegment(sketch, "E762", {"start": v(-1655.86, 391.16) * mm, "end": v(-1655.37, 392.92) * mm});
            skLineSegment(sketch, "E763", {"start": v(-1656.22, 389.37) * mm, "end": v(-1655.86, 391.16) * mm});
            skLineSegment(sketch, "E764", {"start": v(-1656.43, 387.55) * mm, "end": v(-1656.22, 389.37) * mm});
            skLineSegment(sketch, "E765", {"start": v(-1656.5, 385.72) * mm, "end": v(-1656.43, 387.55) * mm});
            skLineSegment(sketch, "E766", {"start": v(-1653.07, 397.9) * mm, "end": v(-1652.05, 399.42) * mm});
            skLineSegment(sketch, "E767", {"start": v(-1646.9, 404.58) * mm, "end": v(-1645.37, 405.6) * mm});
            skLineSegment(sketch, "E768", {"start": v(-1649.68, 402.2) * mm, "end": v(-1648.33, 403.45) * mm});
            skLineSegment(sketch, "E769", {"start": v(-1650.92, 400.86) * mm, "end": v(-1649.68, 402.2) * mm});
            skLineSegment(sketch, "E770", {"start": v(-1648.33, 403.45) * mm, "end": v(-1646.9, 404.58) * mm});
            skLineSegment(sketch, "E771", {"start": v(-1643.77, 406.5) * mm, "end": v(-1642.11, 407.26) * mm});
            skLineSegment(sketch, "E772", {"start": v(-1645.37, 405.6) * mm, "end": v(-1643.77, 406.5) * mm});
            skLineSegment(sketch, "E773", {"start": v(-1642.11, 407.26) * mm, "end": v(-1640.4, 407.9) * mm});
            skLineSegment(sketch, "E774", {"start": v(-1627.58, 378.6) * mm, "end": v(-1628.8, 376.7) * mm});
            skLineSegment(sketch, "E775", {"start": v(-1635.02, 408.96) * mm, "end": v(-1633.19, 409.04) * mm});
            skLineSegment(sketch, "E776", {"start": v(-1633.7, 394.62) * mm, "end": v(-1634.11, 395.02) * mm});
            skLineSegment(sketch, "E777", {"start": v(-1633.97, 391.46) * mm, "end": v(-1633.57, 391.89) * mm});
            skLineSegment(sketch, "E778", {"start": v(-1637.1, 391.56) * mm, "end": v(-1636.62, 391.2) * mm});
            skLineSegment(sketch, "E779", {"start": v(-1636.25, 395.33) * mm, "end": v(-1636.75, 395.07) * mm});
            skLineSegment(sketch, "E780", {"start": v(-1637.45, 392.03) * mm, "end": v(-1637.1, 391.56) * mm});
            skLineSegment(sketch, "E781", {"start": v(-1637.69, 392.56) * mm, "end": v(-1637.45, 392.03) * mm});
            skLineSegment(sketch, "E782", {"start": v(-1637.78, 393.12) * mm, "end": v(-1637.69, 392.56) * mm});
            skLineSegment(sketch, "E783", {"start": v(-1637.72, 393.7) * mm, "end": v(-1637.78, 393.12) * mm});
            skLineSegment(sketch, "E784", {"start": v(-1637.52, 394.24) * mm, "end": v(-1637.72, 393.7) * mm});
            skLineSegment(sketch, "E785", {"start": v(-1637.19, 394.7) * mm, "end": v(-1637.52, 394.24) * mm});
            skLineSegment(sketch, "E786", {"start": v(-1636.75, 395.07) * mm, "end": v(-1637.19, 394.7) * mm});
            skLineSegment(sketch, "E787", {"start": v(-1636.07, 390.96) * mm, "end": v(-1635.48, 390.89) * mm});
            skLineSegment(sketch, "E788", {"start": v(-1636.62, 391.2) * mm, "end": v(-1636.07, 390.96) * mm});
            skLineSegment(sketch, "E789", {"start": v(-1635.7, 395.46) * mm, "end": v(-1636.25, 395.33) * mm});
            skLineSegment(sketch, "E790", {"start": v(-1635.14, 395.45) * mm, "end": v(-1635.7, 395.46) * mm});
            skLineSegment(sketch, "E791", {"start": v(-1634.6, 395.3) * mm, "end": v(-1635.14, 395.45) * mm});
            skLineSegment(sketch, "E792", {"start": v(-1634.11, 395.02) * mm, "end": v(-1634.6, 395.3) * mm});
            skLineSegment(sketch, "E793", {"start": v(-1634.44, 391.14) * mm, "end": v(-1633.97, 391.46) * mm});
            skLineSegment(sketch, "E794", {"start": v(-1634.97, 390.95) * mm, "end": v(-1634.44, 391.14) * mm});
            skLineSegment(sketch, "E795", {"start": v(-1635.48, 390.89) * mm, "end": v(-1634.97, 390.95) * mm});
            skLineSegment(sketch, "E796", {"start": v(-1635.48, 394.2) * mm, "end": v(-1635.48, 390.89) * mm});
            skLineSegment(sketch, "E797", {"start": v(-1636.84, 408.75) * mm, "end": v(-1635.02, 408.96) * mm});
            skLineSegment(sketch, "E798", {"start": v(-1638.63, 408.4) * mm, "end": v(-1636.84, 408.75) * mm});
            skLineSegment(sketch, "E799", {"start": v(-1633.39, 394.13) * mm, "end": v(-1633.7, 394.62) * mm});
            skLineSegment(sketch, "E800", {"start": v(-1633.2, 393.57) * mm, "end": v(-1633.39, 394.13) * mm});
            skLineSegment(sketch, "E801", {"start": v(-1633.18, 392.98) * mm, "end": v(-1633.2, 393.57) * mm});
            skLineSegment(sketch, "E802", {"start": v(-1633.3, 392.41) * mm, "end": v(-1633.18, 392.98) * mm});
            skLineSegment(sketch, "E803", {"start": v(-1633.57, 391.89) * mm, "end": v(-1633.3, 392.41) * mm});
            skLineSegment(sketch, "E804", {"start": v(-1621.22, 384.97) * mm, "end": v(-1623.01, 383.59) * mm});
            skLineSegment(sketch, "E805", {"start": v(-1624.68, 382.06) * mm, "end": v(-1626.2, 380.4) * mm});
            skLineSegment(sketch, "E806", {"start": v(-1626.2, 380.4) * mm, "end": v(-1627.58, 378.6) * mm});
            skLineSegment(sketch, "E807", {"start": v(-1623.01, 383.59) * mm, "end": v(-1624.68, 382.06) * mm});
            skLineSegment(sketch, "E808", {"start": v(-1617.31, 387.22) * mm, "end": v(-1619.32, 386.18) * mm});
            skLineSegment(sketch, "E809", {"start": v(-1619.32, 386.18) * mm, "end": v(-1621.22, 384.97) * mm});
            skLineSegment(sketch, "E810", {"start": v(-1582.76, 374.44) * mm, "end": v(-1583.72, 376.33) * mm});
            skLineSegment(sketch, "E811", {"start": v(-1593.4, 341.3) * mm, "end": v(-1591.61, 342.43) * mm});
            skLineSegment(sketch, "E812", {"start": v(-1606.36, 337.84) * mm, "end": v(-1603.82, 337.96) * mm});
            skLineSegment(sketch, "E813", {"start": v(-1610.86, 338.23) * mm, "end": v(-1608.62, 337.93) * mm});
            skLineSegment(sketch, "E814", {"start": v(-1613.07, 338.72) * mm, "end": v(-1610.86, 338.23) * mm});
            skLineSegment(sketch, "E815", {"start": v(-1615.22, 339.4) * mm, "end": v(-1613.07, 338.72) * mm});
            skLineSegment(sketch, "E816", {"start": v(-1608.62, 337.93) * mm, "end": v(-1606.36, 337.84) * mm});
            skLineSegment(sketch, "E817", {"start": v(-1606.36, 341.14) * mm, "end": v(-1606.36, 337.84) * mm});
            skLineSegment(sketch, "E818", {"start": v(-1598.84, 338.98) * mm, "end": v(-1597.04, 339.6) * mm});
            skLineSegment(sketch, "E819", {"start": v(-1602.24, 338.15) * mm, "end": v(-1600.68, 338.48) * mm});
            skLineSegment(sketch, "E820", {"start": v(-1603.82, 337.96) * mm, "end": v(-1602.24, 338.15) * mm});
            skLineSegment(sketch, "E821", {"start": v(-1600.68, 338.48) * mm, "end": v(-1598.84, 338.98) * mm});
            skLineSegment(sketch, "E822", {"start": v(-1595.28, 340.33) * mm, "end": v(-1593.4, 341.3) * mm});
            skLineSegment(sketch, "E823", {"start": v(-1597.04, 339.6) * mm, "end": v(-1595.28, 340.33) * mm});
            skLineSegment(sketch, "E824", {"start": v(-1586.88, 346.66) * mm, "end": v(-1585.55, 348.31) * mm});
            skLineSegment(sketch, "E825", {"start": v(-1589.93, 343.72) * mm, "end": v(-1588.35, 345.13) * mm});
            skLineSegment(sketch, "E826", {"start": v(-1591.61, 342.43) * mm, "end": v(-1589.93, 343.72) * mm});
            skLineSegment(sketch, "E827", {"start": v(-1588.35, 345.13) * mm, "end": v(-1586.88, 346.66) * mm});
            skLineSegment(sketch, "E828", {"start": v(-1582.43, 353.83) * mm, "end": v(-1581.7, 355.82) * mm});
            skLineSegment(sketch, "E829", {"start": v(-1583.32, 351.9) * mm, "end": v(-1582.43, 353.83) * mm});
            skLineSegment(sketch, "E830", {"start": v(-1584.36, 350.06) * mm, "end": v(-1583.32, 351.9) * mm});
            skLineSegment(sketch, "E831", {"start": v(-1585.55, 348.31) * mm, "end": v(-1584.36, 350.06) * mm});
            skLineSegment(sketch, "E832", {"start": v(-1581.97, 372.47) * mm, "end": v(-1582.76, 374.44) * mm});
            skLineSegment(sketch, "E833", {"start": v(-1581.34, 370.45) * mm, "end": v(-1581.97, 372.47) * mm});
            skLineSegment(sketch, "E834", {"start": v(-1580.87, 368.38) * mm, "end": v(-1581.34, 370.45) * mm});
            skLineSegment(sketch, "E835", {"start": v(-1580.58, 366.28) * mm, "end": v(-1580.87, 368.38) * mm});
            skLineSegment(sketch, "E836", {"start": v(-1580.46, 364.17) * mm, "end": v(-1580.58, 366.28) * mm});
            skLineSegment(sketch, "E837", {"start": v(-1580.51, 362.05) * mm, "end": v(-1580.46, 364.17) * mm});
            skLineSegment(sketch, "E838", {"start": v(-1580.74, 359.94) * mm, "end": v(-1580.51, 362.05) * mm});
            skLineSegment(sketch, "E839", {"start": v(-1581.13, 357.86) * mm, "end": v(-1580.74, 359.94) * mm});
            skLineSegment(sketch, "E840", {"start": v(-1581.7, 355.82) * mm, "end": v(-1581.13, 357.86) * mm});
            skLineSegment(sketch, "E841", {"start": v(-1578.87, 333.13) * mm, "end": v(-1578.4, 332.77) * mm});
            skLineSegment(sketch, "E842", {"start": v(-1576.1, 332.77) * mm, "end": v(-1575.63, 333.14) * mm});
            skLineSegment(sketch, "E843", {"start": v(-1577.25, 335.77) * mm, "end": v(-1577.25, 332.47) * mm});
            skLineSegment(sketch, "E844", {"start": v(-1577.25, 332.47) * mm, "end": v(-1576.65, 332.54) * mm});
            skLineSegment(sketch, "E845", {"start": v(-1577.84, 332.54) * mm, "end": v(-1577.25, 332.47) * mm});
            skLineSegment(sketch, "E846", {"start": v(-1578.4, 332.77) * mm, "end": v(-1577.84, 332.54) * mm});
            skLineSegment(sketch, "E847", {"start": v(-1576.65, 332.54) * mm, "end": v(-1576.1, 332.77) * mm});
            skLineSegment(sketch, "E848", {"start": v(-1576.65, 336.98) * mm, "end": v(-1577.25, 337.05) * mm});
            skLineSegment(sketch, "E849", {"start": v(-1579.23, 333.61) * mm, "end": v(-1578.87, 333.13) * mm});
            skLineSegment(sketch, "E850", {"start": v(-1579.46, 334.16) * mm, "end": v(-1579.23, 333.61) * mm});
            skLineSegment(sketch, "E851", {"start": v(-1579.54, 334.76) * mm, "end": v(-1579.46, 334.16) * mm});
            skLineSegment(sketch, "E852", {"start": v(-1579.46, 335.35) * mm, "end": v(-1579.54, 334.76) * mm});
            skLineSegment(sketch, "E853", {"start": v(-1579.23, 335.9) * mm, "end": v(-1579.46, 335.35) * mm});
            skLineSegment(sketch, "E854", {"start": v(-1578.86, 336.37) * mm, "end": v(-1579.23, 335.9) * mm});
            skLineSegment(sketch, "E855", {"start": v(-1578.39, 336.73) * mm, "end": v(-1578.86, 336.37) * mm});
            skLineSegment(sketch, "E856", {"start": v(-1577.84, 336.96) * mm, "end": v(-1578.39, 336.73) * mm});
            skLineSegment(sketch, "E857", {"start": v(-1577.25, 337.05) * mm, "end": v(-1577.84, 336.96) * mm});
            skLineSegment(sketch, "E858", {"start": v(-1576.1, 336.75) * mm, "end": v(-1576.65, 336.98) * mm});
            skLineSegment(sketch, "E859", {"start": v(-1575.63, 336.38) * mm, "end": v(-1576.1, 336.75) * mm});
            skLineSegment(sketch, "E860", {"start": v(-1575.27, 335.9) * mm, "end": v(-1575.63, 336.38) * mm});
            skLineSegment(sketch, "E861", {"start": v(-1575.03, 335.35) * mm, "end": v(-1575.27, 335.9) * mm});
            skLineSegment(sketch, "E862", {"start": v(-1574.95, 334.75) * mm, "end": v(-1575.03, 335.35) * mm});
            skLineSegment(sketch, "E863", {"start": v(-1575.03, 334.16) * mm, "end": v(-1574.95, 334.75) * mm});
            skLineSegment(sketch, "E864", {"start": v(-1575.26, 333.6) * mm, "end": v(-1575.03, 334.16) * mm});
            skLineSegment(sketch, "E865", {"start": v(-1575.63, 333.14) * mm, "end": v(-1575.26, 333.6) * mm});
            skLineSegment(sketch, "E866", {"start": v(-1590.59, 384.3) * mm, "end": v(-1592.32, 385.52) * mm});
            skLineSegment(sketch, "E867", {"start": v(-1602.21, 389.32) * mm, "end": v(-1604.39, 389.57) * mm});
            skLineSegment(sketch, "E868", {"start": v(-1608.76, 389.54) * mm, "end": v(-1610.93, 389.24) * mm});
            skLineSegment(sketch, "E869", {"start": v(-1610.93, 389.24) * mm, "end": v(-1613.07, 388.77) * mm});
            skLineSegment(sketch, "E870", {"start": v(-1613.07, 388.77) * mm, "end": v(-1615.22, 388.09) * mm});
            skLineSegment(sketch, "E871", {"start": v(-1606.57, 389.65) * mm, "end": v(-1608.76, 389.54) * mm});
            skLineSegment(sketch, "E872", {"start": v(-1604.39, 389.57) * mm, "end": v(-1606.57, 389.65) * mm});
            skLineSegment(sketch, "E873", {"start": v(-1596.06, 387.51) * mm, "end": v(-1598.03, 388.27) * mm});
            skLineSegment(sketch, "E874", {"start": v(-1600.07, 388.87) * mm, "end": v(-1602.21, 389.32) * mm});
            skLineSegment(sketch, "E875", {"start": v(-1598.03, 388.27) * mm, "end": v(-1600.07, 388.87) * mm});
            skLineSegment(sketch, "E876", {"start": v(-1594.15, 386.6) * mm, "end": v(-1596.06, 387.51) * mm});
            skLineSegment(sketch, "E877", {"start": v(-1592.32, 385.52) * mm, "end": v(-1594.15, 386.6) * mm});
            skLineSegment(sketch, "E878", {"start": v(-1586.07, 379.85) * mm, "end": v(-1587.45, 381.45) * mm});
            skLineSegment(sketch, "E879", {"start": v(-1588.96, 382.94) * mm, "end": v(-1590.59, 384.3) * mm});
            skLineSegment(sketch, "E880", {"start": v(-1587.45, 381.45) * mm, "end": v(-1588.96, 382.94) * mm});
            skLineSegment(sketch, "E881", {"start": v(-1584.82, 378.14) * mm, "end": v(-1586.07, 379.85) * mm});
            skLineSegment(sketch, "E882", {"start": v(-1583.72, 376.33) * mm, "end": v(-1584.82, 378.14) * mm});
            skLineSegment(sketch, "E883", {"start": v(-1575.97, 408.75) * mm, "end": v(-1574.18, 408.4) * mm});
            skLineSegment(sketch, "E884", {"start": v(-1576.9, 395.45) * mm, "end": v(-1577.47, 395.46) * mm});
            skLineSegment(sketch, "E885", {"start": v(-1577.25, 390.89) * mm, "end": v(-1576.74, 390.95) * mm});
            skLineSegment(sketch, "E886", {"start": v(-1577.84, 390.96) * mm, "end": v(-1577.25, 390.89) * mm});
            skLineSegment(sketch, "E887", {"start": v(-1578.4, 391.2) * mm, "end": v(-1577.84, 390.96) * mm});
            skLineSegment(sketch, "E888", {"start": v(-1578.86, 391.56) * mm, "end": v(-1578.4, 391.2) * mm});
            skLineSegment(sketch, "E889", {"start": v(-1579.23, 392.03) * mm, "end": v(-1578.86, 391.56) * mm});
            skLineSegment(sketch, "E890", {"start": v(-1579.46, 392.56) * mm, "end": v(-1579.23, 392.03) * mm});
            skLineSegment(sketch, "E891", {"start": v(-1579.55, 393.12) * mm, "end": v(-1579.46, 392.56) * mm});
            skLineSegment(sketch, "E892", {"start": v(-1579.5, 393.7) * mm, "end": v(-1579.55, 393.12) * mm});
            skLineSegment(sketch, "E893", {"start": v(-1579.3, 394.24) * mm, "end": v(-1579.5, 393.7) * mm});
            skLineSegment(sketch, "E894", {"start": v(-1578.96, 394.7) * mm, "end": v(-1579.3, 394.24) * mm});
            skLineSegment(sketch, "E895", {"start": v(-1578.52, 395.07) * mm, "end": v(-1578.96, 394.7) * mm});
            skLineSegment(sketch, "E896", {"start": v(-1578.02, 395.33) * mm, "end": v(-1578.52, 395.07) * mm});
            skLineSegment(sketch, "E897", {"start": v(-1577.47, 395.46) * mm, "end": v(-1578.02, 395.33) * mm});
            skLineSegment(sketch, "E898", {"start": v(-1577.25, 394.2) * mm, "end": v(-1577.25, 390.89) * mm});
            skLineSegment(sketch, "E899", {"start": v(-1576.37, 395.3) * mm, "end": v(-1576.9, 395.45) * mm});
            skLineSegment(sketch, "E900", {"start": v(-1575.88, 395.02) * mm, "end": v(-1576.37, 395.3) * mm});
            skLineSegment(sketch, "E901", {"start": v(-1575.48, 394.62) * mm, "end": v(-1575.88, 395.02) * mm});
            skLineSegment(sketch, "E902", {"start": v(-1575.16, 394.13) * mm, "end": v(-1575.48, 394.62) * mm});
            skLineSegment(sketch, "E903", {"start": v(-1574.98, 393.57) * mm, "end": v(-1575.16, 394.13) * mm});
            skLineSegment(sketch, "E904", {"start": v(-1574.95, 392.98) * mm, "end": v(-1574.98, 393.57) * mm});
            skLineSegment(sketch, "E905", {"start": v(-1575.07, 392.41) * mm, "end": v(-1574.95, 392.98) * mm});
            skLineSegment(sketch, "E906", {"start": v(-1575.34, 391.89) * mm, "end": v(-1575.07, 392.41) * mm});
            skLineSegment(sketch, "E907", {"start": v(-1575.74, 391.46) * mm, "end": v(-1575.34, 391.89) * mm});
            skLineSegment(sketch, "E908", {"start": v(-1576.2, 391.14) * mm, "end": v(-1575.74, 391.46) * mm});
            skLineSegment(sketch, "E909", {"start": v(-1576.74, 390.95) * mm, "end": v(-1576.2, 391.14) * mm});
            skLineSegment(sketch, "E910", {"start": v(-1577.8, 408.96) * mm, "end": v(-1575.97, 408.75) * mm});
            skLineSegment(sketch, "E911", {"start": v(-1579.62, 409.04) * mm, "end": v(-1577.8, 408.96) * mm});
            skLineSegment(sketch, "E912", {"start": v(-1572.41, 407.9) * mm, "end": v(-1570.7, 407.26) * mm});
            skLineSegment(sketch, "E913", {"start": v(-1574.18, 408.4) * mm, "end": v(-1572.41, 407.9) * mm});
            skLineSegment(sketch, "E914", {"start": v(-1570.7, 407.26) * mm, "end": v(-1569.03, 406.5) * mm});
            skLineSegment(sketch, "E915", {"start": v(-1556.22, 240.07) * mm, "end": v(-1556.22, 153.51) * mm});
            skLineSegment(sketch, "E916", {"start": v(-1556.3, 385.72) * mm, "end": v(-1556.3, 240.07) * mm});
            skLineSegment(sketch, "E917", {"start": v(-1552.91, 240.07) * mm, "end": v(-1556.22, 240.07) * mm});
            skLineSegment(sketch, "E918", {"start": v(-1556.3, 240.07) * mm, "end": v(-1556.22, 240.07) * mm});
            skLineSegment(sketch, "E919", {"start": v(-1556.38, 387.55) * mm, "end": v(-1556.3, 385.72) * mm});
            skLineSegment(sketch, "E920", {"start": v(-1563.13, 402.2) * mm, "end": v(-1561.9, 400.86) * mm});
            skLineSegment(sketch, "E921", {"start": v(-1565.91, 404.58) * mm, "end": v(-1564.48, 403.45) * mm});
            skLineSegment(sketch, "E922", {"start": v(-1567.44, 405.6) * mm, "end": v(-1565.91, 404.58) * mm});
            skLineSegment(sketch, "E923", {"start": v(-1564.48, 403.45) * mm, "end": v(-1563.13, 402.2) * mm});
            skLineSegment(sketch, "E924", {"start": v(-1559.74, 397.9) * mm, "end": v(-1558.84, 396.3) * mm});
            skLineSegment(sketch, "E925", {"start": v(-1556.6, 389.37) * mm, "end": v(-1556.38, 387.55) * mm});
            skLineSegment(sketch, "E926", {"start": v(-1556.95, 391.16) * mm, "end": v(-1556.6, 389.37) * mm});
            skLineSegment(sketch, "E927", {"start": v(-1557.44, 392.92) * mm, "end": v(-1556.95, 391.16) * mm});
            skLineSegment(sketch, "E928", {"start": v(-1558.08, 394.64) * mm, "end": v(-1557.44, 392.92) * mm});
            skLineSegment(sketch, "E929", {"start": v(-1558.84, 396.3) * mm, "end": v(-1558.08, 394.64) * mm});
            skLineSegment(sketch, "E930", {"start": v(-1560.76, 399.42) * mm, "end": v(-1559.74, 397.9) * mm});
            skLineSegment(sketch, "E931", {"start": v(-1561.9, 400.86) * mm, "end": v(-1560.76, 399.42) * mm});
            skArc(sketch, "E932", {"start": v(1194.4, 223.65) * mm, "mid": v(1161.1, 191.75) * mm, "end": v(1191.52, 157.1) * mm});
            skFitSpline(sketch, "E933", {"points": [v(1012.03, 162.01) * mm, v(1008, 161.29) * mm, v(1000.32, 159.69) * mm, v(989.49, 156.73) * mm, v(979.85, 153.37) * mm, v(971.39, 149.6) * mm, v(964.14, 145.38) * mm, v(958.22, 140.72) * mm, v(954.77, 136.61) * mm, v(953.43, 134.15) * mm, v(953.19, 133.65) * mm]});
            skLineSegment(sketch, "E934", {"start": v(953.19, 133.65) * mm, "end": v(1012.29, 290.3) * mm});
            skFitSpline(sketch, "E935", {"points": [v(1052.82, 182) * mm, v(1065.38, 182.31) * mm, v(1077.75, 174.17) * mm, v(1086.58, 165.23) * mm]});
            skFitSpline(sketch, "E936", {"points": [v(1019.14, 163.19) * mm, v(1027.52, 172.39) * mm, v(1039, 181.08) * mm, v(1051.41, 181.93) * mm]});
            skLineSegment(sketch, "E937", {"start": v(1093.44, 290.61) * mm, "end": v(1170.37, 133.67) * mm});
            skLineSegment(sketch, "E938", {"start": v(1019.14, 163.19) * mm, "end": v(1012.03, 162.01) * mm});
            skFitSpline(sketch, "E939", {"points": [v(1170.37, 133.67) * mm, v(1170.22, 133.97) * mm, v(1168.56, 137.13) * mm, v(1163.26, 142.9) * mm, v(1152.82, 149.5) * mm, v(1139.06, 155.3) * mm, v(1125, 159.32) * mm, v(1115.58, 161.28) * mm, v(1111.83, 161.96) * mm]});
            skFitSpline(sketch, "E940", {"points": [v(1111.83, 161.96) * mm, v(1109.22, 162.44) * mm, v(1102.94, 163.47) * mm, v(1096.62, 164.26) * mm, v(1092.93, 164.65) * mm]});
            skLineSegment(sketch, "E941", {"start": v(1092.93, 164.65) * mm, "end": v(1086.58, 165.23) * mm});
            skArc(sketch, "E942", {"start": v(1019.65, 290.71) * mm, "mid": v(1052.86, 271.29) * mm, "end": v(1086.07, 290.71) * mm});
            skLineSegment(sketch, "E943", {"start": v(1019.65, 290.71) * mm, "end": v(1019.65, 228.15) * mm});
            skLineSegment(sketch, "E944", {"start": v(1012.29, 290.3) * mm, "end": v(1012.29, 228.15) * mm});
            skLineSegment(sketch, "E945", {"start": v(1019.65, 228.15) * mm, "end": v(1012.29, 228.15) * mm});
            skCircle(sketch, "E946", {"center": v(1052.86, 227.53) * mm, "radius": 15.88 * mm});
            skArc(sketch, "E947", {"start": v(1052.82, 182) * mm, "mid": v(1052.12, 181.98) * mm, "end": v(1051.41, 181.93) * mm});
            skLineSegment(sketch, "E948", {"start": v(1093.44, 290.61) * mm, "end": v(1093.44, 228.15) * mm});
            skLineSegment(sketch, "E949", {"start": v(1086.07, 290.71) * mm, "end": v(1086.07, 228.15) * mm});
            skLineSegment(sketch, "E950", {"start": v(1093.44, 228.15) * mm, "end": v(1086.07, 228.15) * mm});
            skFitSpline(sketch, "E951", {"points": [v(1361.2, 197.1) * mm, v(1362.12, 199.59) * mm, v(1364.43, 204.44) * mm, v(1369.18, 210.91) * mm, v(1375.08, 216.31) * mm, v(1381.86, 220.38) * mm, v(1389.25, 222.95) * mm, v(1394.66, 223.62) * mm, v(1397.47, 223.65) * mm, v(1397.7, 223.65) * mm]});
            skFitSpline(sketch, "E952", {"points": [v(1394.74, 139.5) * mm, v(1393.46, 139.6) * mm, v(1389.62, 140.14) * mm, v(1383.37, 142.04) * mm, v(1376.44, 145.84) * mm, v(1370.34, 151) * mm, v(1365.3, 157.34) * mm, v(1361.51, 164.6) * mm, v(1359.11, 172.5) * mm, v(1358.2, 180.73) * mm, v(1358.62, 186.55) * mm, v(1359.14, 189.55) * mm, v(1359.2, 189.84) * mm]});
            skLineSegment(sketch, "E953", {"start": v(1423.94, 312.79) * mm, "end": v(1219.7, 312.79) * mm});
            skLineSegment(sketch, "E954", {"start": v(1318.82, 271.18) * mm, "end": v(1384.4, 263.34) * mm});
            skLineSegment(sketch, "E955", {"start": v(1386.2, 255.84) * mm, "end": v(1317.98, 264.12) * mm});
            skLineSegment(sketch, "E956", {"start": v(1216.83, 246.24) * mm, "end": v(1419.5, 228.7) * mm});
            skLineSegment(sketch, "E957", {"start": v(1397.7, 223.65) * mm, "end": v(1194.4, 223.65) * mm});
            skLineSegment(sketch, "E958", {"start": v(1191.52, 157.1) * mm, "end": v(1394.74, 139.5) * mm});
            skArc(sketch, "E959", {"start": v(1219.7, 312.79) * mm, "mid": v(1186.4, 280.9) * mm, "end": v(1216.83, 246.24) * mm});
            skCircle(sketch, "E960", {"center": v(1194.4, 190.31) * mm, "radius": 5.08 * mm});
            skCircle(sketch, "E961", {"center": v(1219.7, 279.45) * mm, "radius": 5.08 * mm});
            skLineSegment(sketch, "E962", {"start": v(1359.2, 189.84) * mm, "end": v(1293.85, 188.68) * mm});
            skLineSegment(sketch, "E963", {"start": v(1293.7, 195.8) * mm, "end": v(1361.2, 197.1) * mm});
            skLineSegment(sketch, "E964", {"start": v(1293.85, 188.68) * mm, "end": v(1293.7, 195.8) * mm});
            skLineSegment(sketch, "E965", {"start": v(1317.98, 264.12) * mm, "end": v(1318.82, 271.18) * mm});
            skFitSpline(sketch, "E966", {"points": [v(1419.5, 228.7) * mm, v(1419.1, 228.74) * mm, v(1416.14, 229.04) * mm, v(1410.67, 230.3) * mm, v(1403.56, 233.58) * mm, v(1397.22, 238.3) * mm, v(1391.9, 244.26) * mm, v(1388.33, 250.3) * mm, v(1386.72, 254.3) * mm, v(1386.2, 255.84) * mm]});
            skFitSpline(sketch, "E967", {"points": [v(1384.4, 263.34) * mm, v(1384.2, 264.58) * mm, v(1383.78, 268.58) * mm, v(1383.96, 275.38) * mm, v(1385.7, 283.5) * mm, v(1388.87, 291.11) * mm, v(1393.36, 297.95) * mm, v(1399, 303.75) * mm, v(1405.6, 308.3) * mm, v(1412.87, 311.38) * mm, v(1419.12, 312.62) * mm, v(1422.82, 312.79) * mm, v(1423.94, 312.79) * mm]});
            skLineSegment(sketch, "E968", {"start": v(737.8, -92.59) * mm, "end": v(747.1, -158.94) * mm});
            skLineSegment(sketch, "E969", {"start": v(854, -124.94) * mm, "end": v(855.17, -119.29) * mm});
            skLineSegment(sketch, "E970", {"start": v(823.62, -117.95) * mm, "end": v(854, -124.94) * mm});
            skLineSegment(sketch, "E971", {"start": v(821.82, -125.77) * mm, "end": v(823.62, -117.95) * mm});
            skLineSegment(sketch, "E972", {"start": v(610.89, -106.64) * mm, "end": v(626.41, -162.36) * mm});
            skLineSegment(sketch, "E973", {"start": v(631.25, -129.8) * mm, "end": v(631.1, -86.3) * mm});
            skLineSegment(sketch, "E974", {"start": v(639.28, -86.43) * mm, "end": v(639.28, -129.77) * mm});
            skLineSegment(sketch, "E975", {"start": v(707.77, -129.54) * mm, "end": v(707.48, -86.2) * mm});
            skLineSegment(sketch, "E976", {"start": v(715.65, -86.02) * mm, "end": v(715.8, -129.52) * mm});
            skLineSegment(sketch, "E977", {"start": v(720.85, -162.05) * mm, "end": v(736, -106.22) * mm});
            skLineSegment(sketch, "E978", {"start": v(814.36, -158.17) * mm, "end": v(844, -164.99) * mm});
            skLineSegment(sketch, "E979", {"start": v(842.92, -172.98) * mm, "end": v(812.56, -166) * mm});
            skLineSegment(sketch, "E980", {"start": v(799, -188.35) * mm, "end": v(841.55, -178.93) * mm});
            skLineSegment(sketch, "E981", {"start": v(852.28, -132.78) * mm, "end": v(821.82, -125.77) * mm});
            skLineSegment(sketch, "E982", {"start": v(715.8, -129.52) * mm, "end": v(707.77, -129.54) * mm});
            skLineSegment(sketch, "E983", {"start": v(673.66, -170.81) * mm, "end": v(720.85, -162.05) * mm});
            skLineSegment(sketch, "E984", {"start": v(626.41, -162.36) * mm, "end": v(673.66, -170.81) * mm});
            skLineSegment(sketch, "E985", {"start": v(625.83, -165.62) * mm, "end": v(626.41, -162.36) * mm});
            skLineSegment(sketch, "E986", {"start": v(639.28, -129.77) * mm, "end": v(631.25, -129.8) * mm});
            skLineSegment(sketch, "E987", {"start": v(747.1, -158.94) * mm, "end": v(799, -188.35) * mm});
            skLineSegment(sketch, "E988", {"start": v(812.56, -166) * mm, "end": v(814.36, -158.17) * mm});
            skLineSegment(sketch, "E989", {"start": v(845.16, -150.6) * mm, "end": v(845.53, -148.34) * mm});
            skLineSegment(sketch, "E990", {"start": v(857.6, -163.77) * mm, "end": v(844.9, -164.23) * mm});
            skLineSegment(sketch, "E991", {"start": v(841.55, -178.93) * mm, "end": v(842.92, -172.98) * mm});
            skLineSegment(sketch, "E992", {"start": v(844.87, -164.5) * mm, "end": v(844.9, -164.23) * mm});
            skLineSegment(sketch, "E993", {"start": v(844.67, -164.81) * mm, "end": v(844.87, -164.5) * mm});
            skLineSegment(sketch, "E994", {"start": v(844.35, -164.99) * mm, "end": v(844.67, -164.81) * mm});
            skLineSegment(sketch, "E995", {"start": v(844, -164.99) * mm, "end": v(844.35, -164.99) * mm});
            skLineSegment(sketch, "E996", {"start": v(844.9, -152.88) * mm, "end": v(845.16, -150.6) * mm});
            skLineSegment(sketch, "E997", {"start": v(844.79, -155.17) * mm, "end": v(844.9, -152.88) * mm});
            skLineSegment(sketch, "E998", {"start": v(844.77, -159.7) * mm, "end": v(844.79, -155.17) * mm});
            skLineSegment(sketch, "E999", {"start": v(844.9, -164.23) * mm, "end": v(844.77, -159.7) * mm});
            skLineSegment(sketch, "E1000", {"start": v(850.92, -135.16) * mm, "end": v(852.39, -133.06) * mm});
            skLineSegment(sketch, "E1001", {"start": v(849.6, -137.35) * mm, "end": v(850.92, -135.16) * mm});
            skLineSegment(sketch, "E1002", {"start": v(848.42, -139.62) * mm, "end": v(849.6, -137.35) * mm});
            skLineSegment(sketch, "E1003", {"start": v(847.5, -141.73) * mm, "end": v(848.42, -139.62) * mm});
            skLineSegment(sketch, "E1004", {"start": v(846.7, -143.9) * mm, "end": v(847.5, -141.73) * mm});
            skLineSegment(sketch, "E1005", {"start": v(846.03, -146.1) * mm, "end": v(846.7, -143.9) * mm});
            skLineSegment(sketch, "E1006", {"start": v(845.53, -148.34) * mm, "end": v(846.03, -146.1) * mm});
            skLineSegment(sketch, "E1007", {"start": v(852.39, -133.06) * mm, "end": v(852.28, -132.78) * mm});
            skLineSegment(sketch, "E1008", {"start": v(827.4, -74.74) * mm, "end": v(826.52, -77.34) * mm});
            skLineSegment(sketch, "E1009", {"start": v(848.37, 6.78) * mm, "end": v(791.17, 23.76) * mm});
            skLineSegment(sketch, "E1010", {"start": v(825.95, -57.42) * mm, "end": v(828.5, -57.43) * mm});
            skLineSegment(sketch, "E1011", {"start": v(684.64, 3.23) * mm, "end": v(637.42, -5.37) * mm});
            skLineSegment(sketch, "E1012", {"start": v(731.85, -5.37) * mm, "end": v(684.64, 3.23) * mm});
            skLineSegment(sketch, "E1013", {"start": v(751.83, 5) * mm, "end": v(751.84, -1.1) * mm});
            skLineSegment(sketch, "E1014", {"start": v(650.54, -81.27) * mm, "end": v(718.74, -81.27) * mm});
            skLineSegment(sketch, "E1015", {"start": v(650.4, -37.93) * mm, "end": v(650.54, -81.27) * mm});
            skLineSegment(sketch, "E1016", {"start": v(642.37, -81.43) * mm, "end": v(642.37, -37.93) * mm});
            skLineSegment(sketch, "E1017", {"start": v(637.42, -5.37) * mm, "end": v(622.08, -61.15) * mm});
            skLineSegment(sketch, "E1018", {"start": v(707.48, -86.2) * mm, "end": v(639.28, -86.43) * mm});
            skLineSegment(sketch, "E1019", {"start": v(630.45, -86.03) * mm, "end": v(610.89, -106.64) * mm});
            skLineSegment(sketch, "E1020", {"start": v(622.08, -61.15) * mm, "end": v(641.7, -81.7) * mm});
            skLineSegment(sketch, "E1021", {"start": v(631.1, -86.3) * mm, "end": v(630.45, -86.03) * mm});
            skLineSegment(sketch, "E1022", {"start": v(641.7, -81.7) * mm, "end": v(642.37, -81.43) * mm});
            skLineSegment(sketch, "E1023", {"start": v(683.88, -104.61) * mm, "end": v(684.17, -104.15) * mm});
            skLineSegment(sketch, "E1024", {"start": v(684.1, -107.1) * mm, "end": v(683.78, -106.52) * mm});
            skLineSegment(sketch, "E1025", {"start": v(683.67, -105.23) * mm, "end": v(683.88, -104.61) * mm});
            skLineSegment(sketch, "E1026", {"start": v(683.63, -105.88) * mm, "end": v(683.67, -105.23) * mm});
            skLineSegment(sketch, "E1027", {"start": v(683.78, -106.52) * mm, "end": v(683.63, -105.88) * mm});
            skLineSegment(sketch, "E1028", {"start": v(688.25, -104.6) * mm, "end": v(688.43, -105.12) * mm});
            skLineSegment(sketch, "E1029", {"start": v(688.43, -105.12) * mm, "end": v(688.49, -105.66) * mm});
            skLineSegment(sketch, "E1030", {"start": v(684.55, -107.56) * mm, "end": v(684.1, -107.1) * mm});
            skLineSegment(sketch, "E1031", {"start": v(685.1, -107.9) * mm, "end": v(684.55, -107.56) * mm});
            skLineSegment(sketch, "E1032", {"start": v(685.73, -108.08) * mm, "end": v(685.1, -107.9) * mm});
            skLineSegment(sketch, "E1033", {"start": v(686.39, -108.08) * mm, "end": v(685.73, -108.08) * mm});
            skLineSegment(sketch, "E1034", {"start": v(687.02, -107.9) * mm, "end": v(686.39, -108.08) * mm});
            skLineSegment(sketch, "E1035", {"start": v(687.57, -107.56) * mm, "end": v(687.02, -107.9) * mm});
            skLineSegment(sketch, "E1036", {"start": v(687.96, -107.18) * mm, "end": v(687.57, -107.56) * mm});
            skLineSegment(sketch, "E1037", {"start": v(688.25, -106.72) * mm, "end": v(687.96, -107.18) * mm});
            skLineSegment(sketch, "E1038", {"start": v(688.43, -106.2) * mm, "end": v(688.25, -106.72) * mm});
            skLineSegment(sketch, "E1039", {"start": v(688.49, -105.66) * mm, "end": v(688.43, -106.2) * mm});
            skLineSegment(sketch, "E1040", {"start": v(685.18, -105.66) * mm, "end": v(688.49, -105.66) * mm});
            skLineSegment(sketch, "E1041", {"start": v(687.96, -104.15) * mm, "end": v(688.25, -104.6) * mm});
            skLineSegment(sketch, "E1042", {"start": v(687.57, -103.77) * mm, "end": v(687.96, -104.15) * mm});
            skLineSegment(sketch, "E1043", {"start": v(686.99, -103.42) * mm, "end": v(687.57, -103.77) * mm});
            skLineSegment(sketch, "E1044", {"start": v(686.33, -103.24) * mm, "end": v(686.99, -103.42) * mm});
            skLineSegment(sketch, "E1045", {"start": v(685.65, -103.27) * mm, "end": v(686.33, -103.24) * mm});
            skLineSegment(sketch, "E1046", {"start": v(685, -103.48) * mm, "end": v(685.65, -103.27) * mm});
            skLineSegment(sketch, "E1047", {"start": v(684.55, -103.77) * mm, "end": v(685, -103.48) * mm});
            skLineSegment(sketch, "E1048", {"start": v(684.17, -104.15) * mm, "end": v(684.55, -103.77) * mm});
            skLineSegment(sketch, "E1049", {"start": v(642.37, -37.93) * mm, "end": v(650.4, -37.93) * mm});
            skLineSegment(sketch, "E1050", {"start": v(683.59, -14.4) * mm, "end": v(684.23, -14.19) * mm});
            skLineSegment(sketch, "E1051", {"start": v(684.31, -19) * mm, "end": v(683.68, -18.82) * mm});
            skLineSegment(sketch, "E1052", {"start": v(683.76, -16.58) * mm, "end": v(687.06, -16.58) * mm});
            skLineSegment(sketch, "E1053", {"start": v(682.45, -15.53) * mm, "end": v(682.75, -15.08) * mm});
            skLineSegment(sketch, "E1054", {"start": v(682.24, -16.15) * mm, "end": v(682.45, -15.53) * mm});
            skLineSegment(sketch, "E1055", {"start": v(682.2, -16.8) * mm, "end": v(682.24, -16.15) * mm});
            skLineSegment(sketch, "E1056", {"start": v(682.35, -17.44) * mm, "end": v(682.2, -16.8) * mm});
            skLineSegment(sketch, "E1057", {"start": v(682.67, -18.01) * mm, "end": v(682.35, -17.44) * mm});
            skLineSegment(sketch, "E1058", {"start": v(683.13, -18.48) * mm, "end": v(682.67, -18.01) * mm});
            skLineSegment(sketch, "E1059", {"start": v(683.68, -18.82) * mm, "end": v(683.13, -18.48) * mm});
            skLineSegment(sketch, "E1060", {"start": v(683.13, -14.7) * mm, "end": v(683.59, -14.4) * mm});
            skLineSegment(sketch, "E1061", {"start": v(682.75, -15.08) * mm, "end": v(683.13, -14.7) * mm});
            skLineSegment(sketch, "E1062", {"start": v(686.54, -15.07) * mm, "end": v(686.83, -15.53) * mm});
            skLineSegment(sketch, "E1063", {"start": v(687, -16.04) * mm, "end": v(687.06, -16.58) * mm});
            skLineSegment(sketch, "E1064", {"start": v(686.83, -15.53) * mm, "end": v(687, -16.04) * mm});
            skLineSegment(sketch, "E1065", {"start": v(684.96, -19) * mm, "end": v(684.31, -19) * mm});
            skLineSegment(sketch, "E1066", {"start": v(685.6, -18.82) * mm, "end": v(684.96, -19) * mm});
            skLineSegment(sketch, "E1067", {"start": v(686.15, -18.48) * mm, "end": v(685.6, -18.82) * mm});
            skLineSegment(sketch, "E1068", {"start": v(686.54, -18.1) * mm, "end": v(686.15, -18.48) * mm});
            skLineSegment(sketch, "E1069", {"start": v(686.83, -17.64) * mm, "end": v(686.54, -18.1) * mm});
            skLineSegment(sketch, "E1070", {"start": v(687, -17.13) * mm, "end": v(686.83, -17.64) * mm});
            skLineSegment(sketch, "E1071", {"start": v(687.06, -16.58) * mm, "end": v(687, -17.13) * mm});
            skLineSegment(sketch, "E1072", {"start": v(686.15, -14.69) * mm, "end": v(686.54, -15.07) * mm});
            skLineSegment(sketch, "E1073", {"start": v(685.57, -14.34) * mm, "end": v(686.15, -14.69) * mm});
            skLineSegment(sketch, "E1074", {"start": v(684.91, -14.17) * mm, "end": v(685.57, -14.34) * mm});
            skLineSegment(sketch, "E1075", {"start": v(684.23, -14.19) * mm, "end": v(684.91, -14.17) * mm});
            skLineSegment(sketch, "E1076", {"start": v(747.2, -61.15) * mm, "end": v(731.85, -5.37) * mm});
            skLineSegment(sketch, "E1077", {"start": v(726.9, -37.93) * mm, "end": v(726.9, -81.43) * mm});
            skLineSegment(sketch, "E1078", {"start": v(718.74, -81.27) * mm, "end": v(718.88, -37.93) * mm});
            skLineSegment(sketch, "E1079", {"start": v(811.16, -60.92) * mm, "end": v(813.5, -59.93) * mm});
            skLineSegment(sketch, "E1080", {"start": v(751.98, -56.17) * mm, "end": v(781.75, -96.5) * mm});
            skLineSegment(sketch, "E1081", {"start": v(769.67, -95.8) * mm, "end": v(767.74, -94.45) * mm});
            skLineSegment(sketch, "E1082", {"start": v(747.6, -72.43) * mm, "end": v(737.8, -92.59) * mm});
            skLineSegment(sketch, "E1083", {"start": v(764.17, -91.36) * mm, "end": v(762.55, -89.65) * mm});
            skLineSegment(sketch, "E1084", {"start": v(736, -106.22) * mm, "end": v(716.31, -85.75) * mm});
            skLineSegment(sketch, "E1085", {"start": v(765.9, -92.96) * mm, "end": v(764.17, -91.36) * mm});
            skLineSegment(sketch, "E1086", {"start": v(767.74, -94.45) * mm, "end": v(765.9, -92.96) * mm});
            skLineSegment(sketch, "E1087", {"start": v(727.57, -81.7) * mm, "end": v(747.2, -61.15) * mm});
            skLineSegment(sketch, "E1088", {"start": v(716.31, -85.75) * mm, "end": v(715.65, -86.02) * mm});
            skLineSegment(sketch, "E1089", {"start": v(726.9, -81.43) * mm, "end": v(727.57, -81.7) * mm});
            skLineSegment(sketch, "E1090", {"start": v(754.38, -75.31) * mm, "end": v(753.73, -73.03) * mm});
            skLineSegment(sketch, "E1091", {"start": v(756.04, -79.75) * mm, "end": v(755.15, -77.55) * mm});
            skLineSegment(sketch, "E1092", {"start": v(755.15, -77.55) * mm, "end": v(754.38, -75.31) * mm});
            skLineSegment(sketch, "E1093", {"start": v(757.69, -82.72) * mm, "end": v(756.04, -79.75) * mm});
            skLineSegment(sketch, "E1094", {"start": v(759.49, -85.6) * mm, "end": v(757.69, -82.72) * mm});
            skLineSegment(sketch, "E1095", {"start": v(760.96, -87.67) * mm, "end": v(759.49, -85.6) * mm});
            skLineSegment(sketch, "E1096", {"start": v(762.55, -89.65) * mm, "end": v(760.96, -87.67) * mm});
            skLineSegment(sketch, "E1097", {"start": v(748, -71.8) * mm, "end": v(747.6, -72.43) * mm});
            skLineSegment(sketch, "E1098", {"start": v(748.52, -71.28) * mm, "end": v(748, -71.8) * mm});
            skLineSegment(sketch, "E1099", {"start": v(749.14, -70.9) * mm, "end": v(748.52, -71.28) * mm});
            skLineSegment(sketch, "E1100", {"start": v(749.82, -70.66) * mm, "end": v(749.14, -70.9) * mm});
            skLineSegment(sketch, "E1101", {"start": v(750.57, -70.58) * mm, "end": v(749.82, -70.66) * mm});
            skLineSegment(sketch, "E1102", {"start": v(751.33, -70.67) * mm, "end": v(750.57, -70.58) * mm});
            skLineSegment(sketch, "E1103", {"start": v(752.04, -70.93) * mm, "end": v(751.33, -70.67) * mm});
            skLineSegment(sketch, "E1104", {"start": v(752.67, -71.35) * mm, "end": v(752.04, -70.93) * mm});
            skLineSegment(sketch, "E1105", {"start": v(753.12, -71.84) * mm, "end": v(752.67, -71.35) * mm});
            skLineSegment(sketch, "E1106", {"start": v(753.48, -72.41) * mm, "end": v(753.12, -71.84) * mm});
            skLineSegment(sketch, "E1107", {"start": v(753.73, -73.03) * mm, "end": v(753.48, -72.41) * mm});
            skLineSegment(sketch, "E1108", {"start": v(819.84, -88.74) * mm, "end": v(818.3, -90.43) * mm});
            skLineSegment(sketch, "E1109", {"start": v(789.3, -90.8) * mm, "end": v(789.7, -88.28) * mm});
            skLineSegment(sketch, "E1110", {"start": v(800.05, -101) * mm, "end": v(797.56, -101.54) * mm});
            skLineSegment(sketch, "E1111", {"start": v(784.88, -101.7) * mm, "end": v(782.59, -101.24) * mm});
            skLineSegment(sketch, "E1112", {"start": v(781.75, -96.5) * mm, "end": v(789.07, -93.33) * mm});
            skLineSegment(sketch, "E1113", {"start": v(771.69, -97.03) * mm, "end": v(769.67, -95.8) * mm});
            skLineSegment(sketch, "E1114", {"start": v(773.76, -98.14) * mm, "end": v(771.69, -97.03) * mm});
            skLineSegment(sketch, "E1115", {"start": v(775.9, -99.12) * mm, "end": v(773.76, -98.14) * mm});
            skLineSegment(sketch, "E1116", {"start": v(778.1, -99.97) * mm, "end": v(775.9, -99.12) * mm});
            skLineSegment(sketch, "E1117", {"start": v(780.32, -100.67) * mm, "end": v(778.1, -99.97) * mm});
            skLineSegment(sketch, "E1118", {"start": v(782.59, -101.24) * mm, "end": v(780.32, -100.67) * mm});
            skLineSegment(sketch, "E1119", {"start": v(787.4, -102) * mm, "end": v(784.88, -101.7) * mm});
            skLineSegment(sketch, "E1120", {"start": v(789.95, -102.14) * mm, "end": v(787.4, -102) * mm});
            skLineSegment(sketch, "E1121", {"start": v(792.5, -102.1) * mm, "end": v(789.95, -102.14) * mm});
            skLineSegment(sketch, "E1122", {"start": v(795.04, -101.9) * mm, "end": v(792.5, -102.1) * mm});
            skLineSegment(sketch, "E1123", {"start": v(797.56, -101.54) * mm, "end": v(795.04, -101.9) * mm});
            skLineSegment(sketch, "E1124", {"start": v(789.07, -93.33) * mm, "end": v(789.3, -90.8) * mm});
            skLineSegment(sketch, "E1125", {"start": v(813.13, -94.93) * mm, "end": v(811.24, -96.21) * mm});
            skLineSegment(sketch, "E1126", {"start": v(802.5, -100.3) * mm, "end": v(800.05, -101) * mm});
            skLineSegment(sketch, "E1127", {"start": v(804.9, -99.45) * mm, "end": v(802.5, -100.3) * mm});
            skLineSegment(sketch, "E1128", {"start": v(807.23, -98.43) * mm, "end": v(804.9, -99.45) * mm});
            skLineSegment(sketch, "E1129", {"start": v(809.27, -97.38) * mm, "end": v(807.23, -98.43) * mm});
            skLineSegment(sketch, "E1130", {"start": v(811.24, -96.21) * mm, "end": v(809.27, -97.38) * mm});
            skLineSegment(sketch, "E1131", {"start": v(814.95, -93.54) * mm, "end": v(813.13, -94.93) * mm});
            skLineSegment(sketch, "E1132", {"start": v(816.67, -92.03) * mm, "end": v(814.95, -93.54) * mm});
            skLineSegment(sketch, "E1133", {"start": v(818.3, -90.43) * mm, "end": v(816.67, -92.03) * mm});
            skLineSegment(sketch, "E1134", {"start": v(796.97, -72.21) * mm, "end": v(798.42, -70.45) * mm});
            skLineSegment(sketch, "E1135", {"start": v(794.14, -76.43) * mm, "end": v(795.48, -74.28) * mm});
            skLineSegment(sketch, "E1136", {"start": v(792.94, -78.67) * mm, "end": v(794.14, -76.43) * mm});
            skLineSegment(sketch, "E1137", {"start": v(791.9, -81) * mm, "end": v(792.94, -78.67) * mm});
            skLineSegment(sketch, "E1138", {"start": v(791, -83.37) * mm, "end": v(791.9, -81) * mm});
            skLineSegment(sketch, "E1139", {"start": v(790.27, -85.8) * mm, "end": v(791, -83.37) * mm});
            skLineSegment(sketch, "E1140", {"start": v(789.7, -88.28) * mm, "end": v(790.27, -85.8) * mm});
            skLineSegment(sketch, "E1141", {"start": v(795.48, -74.28) * mm, "end": v(796.97, -72.21) * mm});
            skLineSegment(sketch, "E1142", {"start": v(821.27, -86.95) * mm, "end": v(819.84, -88.74) * mm});
            skLineSegment(sketch, "E1143", {"start": v(822.83, -84.7) * mm, "end": v(821.27, -86.95) * mm});
            skLineSegment(sketch, "E1144", {"start": v(824.23, -82.33) * mm, "end": v(822.83, -84.7) * mm});
            skLineSegment(sketch, "E1145", {"start": v(825.46, -79.88) * mm, "end": v(824.23, -82.33) * mm});
            skLineSegment(sketch, "E1146", {"start": v(826.52, -77.34) * mm, "end": v(825.46, -79.88) * mm});
            skLineSegment(sketch, "E1147", {"start": v(809.1, -61.94) * mm, "end": v(811.16, -60.92) * mm});
            skLineSegment(sketch, "E1148", {"start": v(807.13, -63.08) * mm, "end": v(809.1, -61.94) * mm});
            skLineSegment(sketch, "E1149", {"start": v(805.21, -64.34) * mm, "end": v(807.13, -63.08) * mm});
            skLineSegment(sketch, "E1150", {"start": v(803.38, -65.7) * mm, "end": v(805.21, -64.34) * mm});
            skLineSegment(sketch, "E1151", {"start": v(801.64, -67.19) * mm, "end": v(803.38, -65.7) * mm});
            skLineSegment(sketch, "E1152", {"start": v(799.98, -68.77) * mm, "end": v(801.64, -67.19) * mm});
            skLineSegment(sketch, "E1153", {"start": v(798.42, -70.45) * mm, "end": v(799.98, -68.77) * mm});
            skLineSegment(sketch, "E1154", {"start": v(783, -9.1) * mm, "end": v(752.6, -9.13) * mm});
            skLineSegment(sketch, "E1155", {"start": v(751.84, -1.1) * mm, "end": v(782.99, -1.08) * mm});
            skLineSegment(sketch, "E1156", {"start": v(783.02, -50.38) * mm, "end": v(751.86, -50.4) * mm});
            skLineSegment(sketch, "E1157", {"start": v(751.76, -42.38) * mm, "end": v(783.02, -42.35) * mm});
            skLineSegment(sketch, "E1158", {"start": v(754.86, -27.99) * mm, "end": v(754.7, -30.29) * mm});
            skLineSegment(sketch, "E1159", {"start": v(718.88, -37.93) * mm, "end": v(726.9, -37.93) * mm});
            skLineSegment(sketch, "E1160", {"start": v(751.86, -50.4) * mm, "end": v(751.98, -56.17) * mm});
            skLineSegment(sketch, "E1161", {"start": v(751.6, -42.12) * mm, "end": v(751.76, -42.38) * mm});
            skLineSegment(sketch, "E1162", {"start": v(752.55, -39.75) * mm, "end": v(751.6, -42.12) * mm});
            skLineSegment(sketch, "E1163", {"start": v(753.35, -37.32) * mm, "end": v(752.55, -39.75) * mm});
            skLineSegment(sketch, "E1164", {"start": v(753.98, -34.84) * mm, "end": v(753.35, -37.32) * mm});
            skLineSegment(sketch, "E1165", {"start": v(754.4, -32.58) * mm, "end": v(753.98, -34.84) * mm});
            skLineSegment(sketch, "E1166", {"start": v(754.7, -30.29) * mm, "end": v(754.4, -32.58) * mm});
            skLineSegment(sketch, "E1167", {"start": v(739.6, -13.38) * mm, "end": v(751.87, -10.07) * mm});
            skLineSegment(sketch, "E1168", {"start": v(732.45, -2.13) * mm, "end": v(731.85, -5.37) * mm});
            skLineSegment(sketch, "E1169", {"start": v(753.04, -14.53) * mm, "end": v(754.05, -19.03) * mm});
            skLineSegment(sketch, "E1170", {"start": v(754.84, -25.73) * mm, "end": v(754.86, -27.99) * mm});
            skLineSegment(sketch, "E1171", {"start": v(754.7, -23.48) * mm, "end": v(754.84, -25.73) * mm});
            skLineSegment(sketch, "E1172", {"start": v(754.44, -21.25) * mm, "end": v(754.7, -23.48) * mm});
            skLineSegment(sketch, "E1173", {"start": v(754.05, -19.03) * mm, "end": v(754.44, -21.25) * mm});
            skLineSegment(sketch, "E1174", {"start": v(751.88, -9.67) * mm, "end": v(751.87, -10.07) * mm});
            skLineSegment(sketch, "E1175", {"start": v(752.09, -9.31) * mm, "end": v(751.88, -9.67) * mm});
            skLineSegment(sketch, "E1176", {"start": v(752.33, -9.19) * mm, "end": v(752.09, -9.31) * mm});
            skLineSegment(sketch, "E1177", {"start": v(752.6, -9.13) * mm, "end": v(752.33, -9.19) * mm});
            skLineSegment(sketch, "E1178", {"start": v(751.87, -10.07) * mm, "end": v(753.04, -14.53) * mm});
            skLineSegment(sketch, "E1179", {"start": v(783.02, -42.35) * mm, "end": v(783.02, -50.38) * mm});
            skLineSegment(sketch, "E1180", {"start": v(823.4, -57.59) * mm, "end": v(825.95, -57.42) * mm});
            skLineSegment(sketch, "E1181", {"start": v(820.87, -57.92) * mm, "end": v(823.4, -57.59) * mm});
            skLineSegment(sketch, "E1182", {"start": v(818.38, -58.43) * mm, "end": v(820.87, -57.92) * mm});
            skLineSegment(sketch, "E1183", {"start": v(815.92, -59.1) * mm, "end": v(818.38, -58.43) * mm});
            skLineSegment(sketch, "E1184", {"start": v(813.5, -59.93) * mm, "end": v(815.92, -59.1) * mm});
            skLineSegment(sketch, "E1185", {"start": v(782.99, -1.08) * mm, "end": v(783, -9.1) * mm});
            skLineSegment(sketch, "E1186", {"start": v(791.17, 23.76) * mm, "end": v(751.83, 5) * mm});
            skLineSegment(sketch, "E1187", {"start": v(872.35, -55.78) * mm, "end": v(848.37, 6.78) * mm});
            skLineSegment(sketch, "E1188", {"start": v(867.34, -77.62) * mm, "end": v(872.35, -55.78) * mm});
            skLineSegment(sketch, "E1189", {"start": v(840.57, -59.83) * mm, "end": v(842.76, -60.7) * mm});
            skLineSegment(sketch, "E1190", {"start": v(855.17, -119.29) * mm, "end": v(835.24, -73.3) * mm});
            skLineSegment(sketch, "E1191", {"start": v(854.6, -69.23) * mm, "end": v(856.06, -70.8) * mm});
            skLineSegment(sketch, "E1192", {"start": v(835.24, -73.3) * mm, "end": v(827.4, -74.74) * mm});
            skLineSegment(sketch, "E1193", {"start": v(852.8, -67.46) * mm, "end": v(854.6, -69.23) * mm});
            skLineSegment(sketch, "E1194", {"start": v(850.89, -65.79) * mm, "end": v(852.8, -67.46) * mm});
            skLineSegment(sketch, "E1195", {"start": v(848.9, -64.21) * mm, "end": v(850.89, -65.79) * mm});
            skLineSegment(sketch, "E1196", {"start": v(846.93, -62.9) * mm, "end": v(848.9, -64.21) * mm});
            skLineSegment(sketch, "E1197", {"start": v(844.88, -61.74) * mm, "end": v(846.93, -62.9) * mm});
            skLineSegment(sketch, "E1198", {"start": v(842.76, -60.7) * mm, "end": v(844.88, -61.74) * mm});
            skLineSegment(sketch, "E1199", {"start": v(858.65, -74.07) * mm, "end": v(859.77, -75.8) * mm});
            skLineSegment(sketch, "E1200", {"start": v(867.1, -78.32) * mm, "end": v(867.34, -77.62) * mm});
            skLineSegment(sketch, "E1201", {"start": v(866.7, -78.95) * mm, "end": v(867.1, -78.32) * mm});
            skLineSegment(sketch, "E1202", {"start": v(866.18, -79.46) * mm, "end": v(866.7, -78.95) * mm});
            skLineSegment(sketch, "E1203", {"start": v(865.57, -79.84) * mm, "end": v(866.18, -79.46) * mm});
            skLineSegment(sketch, "E1204", {"start": v(864.86, -80.1) * mm, "end": v(865.57, -79.84) * mm});
            skLineSegment(sketch, "E1205", {"start": v(864.1, -80.18) * mm, "end": v(864.86, -80.1) * mm});
            skLineSegment(sketch, "E1206", {"start": v(863.35, -80.08) * mm, "end": v(864.1, -80.18) * mm});
            skLineSegment(sketch, "E1207", {"start": v(862.64, -79.82) * mm, "end": v(863.35, -80.08) * mm});
            skLineSegment(sketch, "E1208", {"start": v(862, -79.4) * mm, "end": v(862.64, -79.82) * mm});
            skLineSegment(sketch, "E1209", {"start": v(861.57, -78.94) * mm, "end": v(862, -79.4) * mm});
            skLineSegment(sketch, "E1210", {"start": v(859.77, -75.8) * mm, "end": v(861.57, -78.94) * mm});
            skLineSegment(sketch, "E1211", {"start": v(857.47, -72.39) * mm, "end": v(858.65, -74.07) * mm});
            skLineSegment(sketch, "E1212", {"start": v(856.06, -70.8) * mm, "end": v(857.47, -72.39) * mm});
            skLineSegment(sketch, "E1213", {"start": v(838.33, -59.09) * mm, "end": v(840.57, -59.83) * mm});
            skLineSegment(sketch, "E1214", {"start": v(836.06, -58.46) * mm, "end": v(838.33, -59.09) * mm});
            skLineSegment(sketch, "E1215", {"start": v(833.56, -57.95) * mm, "end": v(836.06, -58.46) * mm});
            skLineSegment(sketch, "E1216", {"start": v(831.04, -57.6) * mm, "end": v(833.56, -57.95) * mm});
            skLineSegment(sketch, "E1217", {"start": v(828.5, -57.43) * mm, "end": v(831.04, -57.6) * mm});
            skFitSpline(sketch, "E1218", {"points": [v(1445.3, -199.6) * mm, v(1432.04, -194.5) * mm, v(1405.54, -184.32) * mm, v(1379.04, -194.5) * mm, v(1365.8, -199.6) * mm]});
            skLineSegment(sketch, "E1219", {"start": v(1372.14, -233.66) * mm, "end": v(1438.94, -233.66) * mm});
            skLineSegment(sketch, "E1220", {"start": v(1365.8, -226.41) * mm, "end": v(1372.14, -226.41) * mm});
            skLineSegment(sketch, "E1221", {"start": v(1365.8, -199.6) * mm, "end": v(1357.28, -233.66) * mm});
            skLineSegment(sketch, "E1222", {"start": v(1365.8, -233.66) * mm, "end": v(1365.8, -226.41) * mm});
            skLineSegment(sketch, "E1223", {"start": v(1357.28, -233.66) * mm, "end": v(1365.8, -233.66) * mm});
            skLineSegment(sketch, "E1224", {"start": v(1405.54, -199.6) * mm, "end": v(1405.54, -197.05) * mm});
            skLineSegment(sketch, "E1225", {"start": v(1405.54, -199.6) * mm, "end": v(1403, -199.6) * mm});
            skLineSegment(sketch, "E1226", {"start": v(1405.54, -199.6) * mm, "end": v(1405.54, -202.13) * mm});
            skLineSegment(sketch, "E1227", {"start": v(1405.54, -199.6) * mm, "end": v(1408.08, -199.6) * mm});
            skLineSegment(sketch, "E1228", {"start": v(1405.54, -194.51) * mm, "end": v(1405.54, -190.7) * mm});
            skLineSegment(sketch, "E1229", {"start": v(1400.46, -199.6) * mm, "end": v(1396.65, -199.6) * mm});
            skLineSegment(sketch, "E1230", {"start": v(1405.54, -204.67) * mm, "end": v(1405.54, -208.48) * mm});
            skLineSegment(sketch, "E1231", {"start": v(1410.62, -199.6) * mm, "end": v(1414.43, -199.6) * mm});
            skCircle(sketch, "E1232", {"center": v(1405.54, -199.6) * mm, "radius": 6.35 * mm});
            skLineSegment(sketch, "E1233", {"start": v(1372.14, -226.41) * mm, "end": v(1372.14, -233.66) * mm});
            skLineSegment(sketch, "E1234", {"start": v(1453.8, -233.66) * mm, "end": v(1445.3, -199.6) * mm});
            skLineSegment(sketch, "E1235", {"start": v(1445.28, -233.66) * mm, "end": v(1453.8, -233.66) * mm});
            skLineSegment(sketch, "E1236", {"start": v(1438.94, -233.66) * mm, "end": v(1438.94, -226.41) * mm});
            skLineSegment(sketch, "E1237", {"start": v(1445.28, -226.41) * mm, "end": v(1445.28, -233.66) * mm});
            skLineSegment(sketch, "E1238", {"start": v(1438.94, -226.41) * mm, "end": v(1445.28, -226.41) * mm});
            skLineSegment(sketch, "E1239", {"start": v(1406.01, -336.54) * mm, "end": v(1446.8, -350.73) * mm});
            skLineSegment(sketch, "E1240", {"start": v(1467.85, -292.16) * mm, "end": v(1406.37, -270.04) * mm});
            skLineSegment(sketch, "E1241", {"start": v(1358.93, -263.28) * mm, "end": v(1358.93, -342.65) * mm});
            skLineSegment(sketch, "E1242", {"start": v(1366.57, -336.54) * mm, "end": v(1406.01, -336.54) * mm});
            skLineSegment(sketch, "E1243", {"start": v(1366.57, -342.6) * mm, "end": v(1366.57, -336.54) * mm});
            skLineSegment(sketch, "E1244", {"start": v(1358.93, -342.65) * mm, "end": v(1366.57, -342.6) * mm});
            skLineSegment(sketch, "E1245", {"start": v(1406.37, -270.04) * mm, "end": v(1366.57, -270.04) * mm});
            skLineSegment(sketch, "E1246", {"start": v(1366.57, -263.28) * mm, "end": v(1358.93, -263.28) * mm});
            skLineSegment(sketch, "E1247", {"start": v(1366.57, -270.04) * mm, "end": v(1366.57, -263.28) * mm});
            skArc(sketch, "E1248", {"start": v(1477.53, -291.9) * mm, "mid": v(1454.98, -322.11) * mm, "end": v(1452.33, -359.72) * mm});
            skLineSegment(sketch, "E1249", {"start": v(1444.55, -356.9) * mm, "end": v(1452.33, -359.72) * mm});
            skLineSegment(sketch, "E1250", {"start": v(1446.8, -350.73) * mm, "end": v(1444.55, -356.9) * mm});
            skLineSegment(sketch, "E1251", {"start": v(1478.47, -289.34) * mm, "end": v(1470.02, -286.2) * mm});
            skLineSegment(sketch, "E1252", {"start": v(1470.02, -286.2) * mm, "end": v(1467.85, -292.16) * mm});
            skLineSegment(sketch, "E1253", {"start": v(1477.53, -291.9) * mm, "end": v(1478.47, -289.34) * mm});
            skLineSegment(sketch, "E1254", {"start": v(1576.93, -244.48) * mm, "end": v(1576.93, -241.94) * mm});
            skLineSegment(sketch, "E1255", {"start": v(1576.93, -244.48) * mm, "end": v(1574.39, -244.48) * mm});
            skLineSegment(sketch, "E1256", {"start": v(1576.93, -244.48) * mm, "end": v(1576.93, -247.02) * mm});
            skLineSegment(sketch, "E1257", {"start": v(1576.93, -244.48) * mm, "end": v(1579.47, -244.48) * mm});
            skLineSegment(sketch, "E1258", {"start": v(1576.93, -239.4) * mm, "end": v(1576.93, -235.6) * mm});
            skLineSegment(sketch, "E1259", {"start": v(1571.85, -244.48) * mm, "end": v(1568.04, -244.48) * mm});
            skLineSegment(sketch, "E1260", {"start": v(1576.93, -249.56) * mm, "end": v(1576.93, -253.37) * mm});
            skLineSegment(sketch, "E1261", {"start": v(1582, -244.48) * mm, "end": v(1585.82, -244.48) * mm});
            skLineSegment(sketch, "E1262", {"start": v(1513.43, -263.2) * mm, "end": v(1576.93, -263.2) * mm});
            skLineSegment(sketch, "E1263", {"start": v(1580.87, -222.9) * mm, "end": v(1530.69, -209.96) * mm});
            skCircle(sketch, "E1264", {"center": v(1576.93, -244.48) * mm, "radius": 4.76 * mm});
            skArc(sketch, "E1265", {"start": v(1496.28, -263.76) * mm, "mid": v(1513.6, -243.79) * mm, "end": v(1495.72, -224.33) * mm});
            skLineSegment(sketch, "E1266", {"start": v(1537.1, -211.62) * mm, "end": v(1537.1, -263.2) * mm});
            skLineSegment(sketch, "E1267", {"start": v(1496.28, -265.92) * mm, "end": v(1513.43, -265.92) * mm});
            skLineSegment(sketch, "E1268", {"start": v(1496.28, -263.76) * mm, "end": v(1496.28, -265.92) * mm});
            skLineSegment(sketch, "E1269", {"start": v(1513.43, -265.92) * mm, "end": v(1513.43, -263.2) * mm});
            skLineSegment(sketch, "E1270", {"start": v(1513.82, -211.35) * mm, "end": v(1506.13, -210.9) * mm});
            skLineSegment(sketch, "E1271", {"start": v(1506.13, -210.9) * mm, "end": v(1506.13, -222.63) * mm});
            skLineSegment(sketch, "E1272", {"start": v(1502.68, -222.63) * mm, "end": v(1502.68, -210.44) * mm});
            skLineSegment(sketch, "E1273", {"start": v(1499.5, -209.96) * mm, "end": v(1495.72, -224.33) * mm});
            skLineSegment(sketch, "E1274", {"start": v(1506.13, -222.63) * mm, "end": v(1502.68, -222.63) * mm});
            skLineSegment(sketch, "E1275", {"start": v(1502.68, -210.44) * mm, "end": v(1499.5, -209.96) * mm});
            skLineSegment(sketch, "E1276", {"start": v(1528.5, -210.32) * mm, "end": v(1528.5, -222.63) * mm});
            skLineSegment(sketch, "E1277", {"start": v(1525.18, -222.63) * mm, "end": v(1525.18, -210.8) * mm});
            skLineSegment(sketch, "E1278", {"start": v(1528.5, -222.63) * mm, "end": v(1525.18, -222.63) * mm});
            skLineSegment(sketch, "E1279", {"start": v(1525.18, -210.8) * mm, "end": v(1513.82, -211.35) * mm});
            skLineSegment(sketch, "E1280", {"start": v(1530.69, -209.96) * mm, "end": v(1528.5, -210.32) * mm});
            skArc(sketch, "E1281", {"start": v(1576.93, -266.42) * mm, "mid": v(1598.77, -246.46) * mm, "end": v(1580.87, -222.9) * mm});
            skLineSegment(sketch, "E1282", {"start": v(1576.93, -263.2) * mm, "end": v(1576.93, -266.42) * mm});
            skLineSegment(sketch, "E1283", {"start": v(1510.63, -407.35) * mm, "end": v(1612.23, -407.35) * mm});
            skLineSegment(sketch, "E1284", {"start": v(1621.38, -326.9) * mm, "end": v(1545.18, -301.65) * mm});
            skArc(sketch, "E1285", {"start": v(1476.34, -409.25) * mm, "mid": v(1511, -369.32) * mm, "end": v(1475.24, -330.39) * mm});
            skLineSegment(sketch, "E1286", {"start": v(1476.34, -413.57) * mm, "end": v(1510.63, -413.57) * mm});
            skLineSegment(sketch, "E1287", {"start": v(1476.34, -409.25) * mm, "end": v(1476.34, -413.57) * mm});
            skLineSegment(sketch, "E1288", {"start": v(1510.63, -413.57) * mm, "end": v(1510.63, -407.35) * mm});
            skLineSegment(sketch, "E1289", {"start": v(1489.16, -302.61) * mm, "end": v(1482.81, -301.65) * mm});
            skLineSegment(sketch, "E1290", {"start": v(1482.81, -301.65) * mm, "end": v(1475.24, -330.39) * mm});
            skLineSegment(sketch, "E1291", {"start": v(1540.8, -302.36) * mm, "end": v(1540.8, -326.99) * mm});
            skLineSegment(sketch, "E1292", {"start": v(1534.16, -326.99) * mm, "end": v(1534.16, -303.35) * mm});
            skLineSegment(sketch, "E1293", {"start": v(1496.06, -303.54) * mm, "end": v(1496.06, -326.99) * mm});
            skLineSegment(sketch, "E1294", {"start": v(1489.16, -326.99) * mm, "end": v(1489.16, -302.61) * mm});
            skLineSegment(sketch, "E1295", {"start": v(1496.06, -326.99) * mm, "end": v(1489.16, -326.99) * mm});
            skLineSegment(sketch, "E1296", {"start": v(1540.8, -326.99) * mm, "end": v(1534.16, -326.99) * mm});
            skLineSegment(sketch, "E1297", {"start": v(1534.16, -303.35) * mm, "end": v(1511.45, -304.44) * mm});
            skLineSegment(sketch, "E1298", {"start": v(1511.45, -304.44) * mm, "end": v(1496.06, -303.54) * mm});
            skLineSegment(sketch, "E1299", {"start": v(1545.18, -301.65) * mm, "end": v(1540.8, -302.36) * mm});
            skArc(sketch, "E1300", {"start": v(1612.23, -413.74) * mm, "mid": v(1656.27, -374.48) * mm, "end": v(1621.38, -326.9) * mm});
            skLineSegment(sketch, "E1301", {"start": v(1557.73, -305.81) * mm, "end": v(1557.73, -407.35) * mm});
            skLineSegment(sketch, "E1302", {"start": v(1612.64, -369.88) * mm, "end": v(1612.64, -367.34) * mm});
            skLineSegment(sketch, "E1303", {"start": v(1612.64, -369.88) * mm, "end": v(1610.1, -369.88) * mm});
            skLineSegment(sketch, "E1304", {"start": v(1612.64, -369.88) * mm, "end": v(1612.64, -372.42) * mm});
            skLineSegment(sketch, "E1305", {"start": v(1612.64, -369.88) * mm, "end": v(1615.18, -369.88) * mm});
            skLineSegment(sketch, "E1306", {"start": v(1612.64, -364.8) * mm, "end": v(1612.64, -360.99) * mm});
            skLineSegment(sketch, "E1307", {"start": v(1607.56, -369.88) * mm, "end": v(1603.75, -369.88) * mm});
            skLineSegment(sketch, "E1308", {"start": v(1612.64, -374.96) * mm, "end": v(1612.64, -378.77) * mm});
            skLineSegment(sketch, "E1309", {"start": v(1617.72, -369.88) * mm, "end": v(1621.53, -369.88) * mm});
            skCircle(sketch, "E1310", {"center": v(1612.64, -369.88) * mm, "radius": 9.53 * mm});
            skLineSegment(sketch, "E1311", {"start": v(1612.23, -407.35) * mm, "end": v(1612.23, -413.74) * mm});
            skSolve(sketch);
        }
        {
            var Q0;
            Q0=makeQuery(id+"F0.imprint","IMPRINT",FACE,{"disambiguationData":[TD([[makeQuery(id+"F0.imprint","IMPRINT",EDGE,{"derivedFrom":sQuery(id+"F0.wireOp",EDGE,"E1011")}),1.0]])]});
            var Q1;
            Q1=makeQuery(id+"F0.imprint","IMPRINT",FACE,{"disambiguationData":[TD([[makeQuery(id+"F0.imprint","IMPRINT",EDGE,{"derivedFrom":sQuery(id+"F0.wireOp",EDGE,"E1009")}),1.0]])]});
            var Q2;
            Q2=makeQuery(id+"F0.imprint","IMPRINT",FACE,{"disambiguationData":[TD([[makeQuery(id+"F0.imprint","IMPRINT",EDGE,{"derivedFrom":sQuery(id+"F0.wireOp",EDGE,"E968")}),1.0]])]});
            var Q3;
            Q3=makeQuery(id+"F0.imprint","IMPRINT",FACE,{"disambiguationData":[TD([[makeQuery(id+"F0.imprint","IMPRINT",EDGE,{"derivedFrom":sQuery(id+"F0.wireOp",EDGE,"E972")}),1.0]])]});
            extrude(context, id + "F1", {"entities" : qUnion([Q0, Q1, Q2, Q3]), "depth" : 6.35 * mm});
        }
    });
